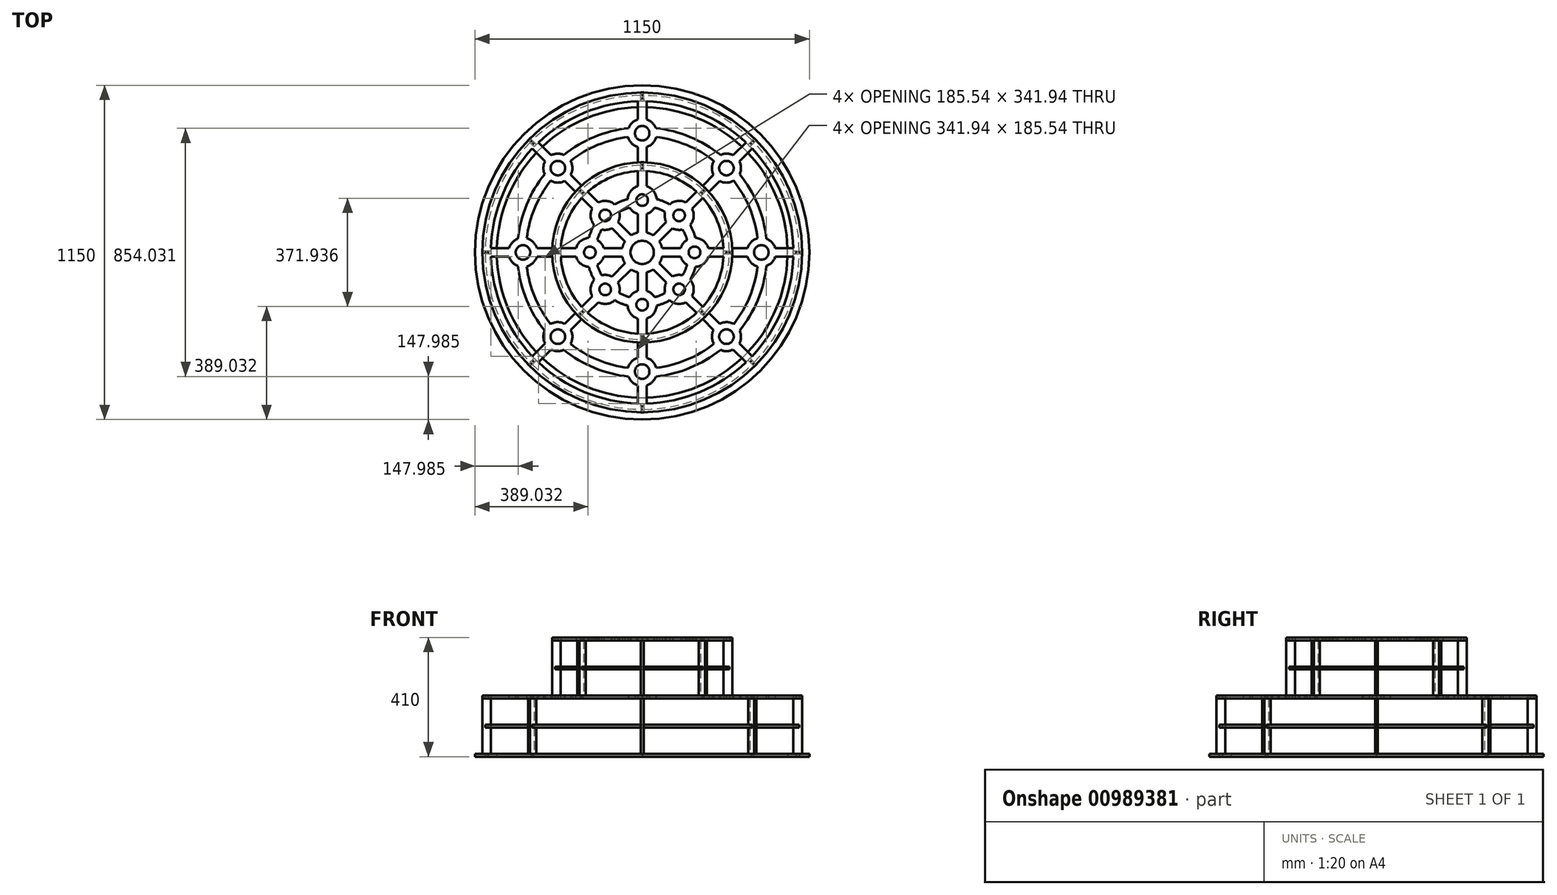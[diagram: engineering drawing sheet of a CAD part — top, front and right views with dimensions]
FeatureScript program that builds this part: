
annotation { "Feature Type Name" : "Feature", "Feature Type Description" : "" }
export const myFeature = defineFeature(function(context is Context, id is Id, definition is map)
    precondition{}
    {
        {
            var Q0;
            Q0=qCreatedBy(makeId("Top.planeOp"),FACE);
            cPlane(context, id + "F0", {"entities" : qUnion([Q0]), "cplaneType" : CPlaneType.OFFSET, "offset" : 200 * mm, "width" : 150 * mm, "height" : 150 * mm});
        }
        {
            var Q0;
            Q0=qCreatedBy(makeId("Top.planeOp"),FACE);
            cPlane(context, id + "F1", {"entities" : qUnion([Q0]), "cplaneType" : CPlaneType.OFFSET, "offset" : 200 * mm, "oppositeDirection" : true, "width" : 150 * mm, "height" : 150 * mm});
        }
        {
            var Q0;
            Q0=qCreatedBy(makeId("Top.planeOp"),FACE);
            cPlane(context, id + "F2", {"entities" : qUnion([Q0]), "cplaneType" : CPlaneType.OFFSET, "offset" : 100 * mm, "oppositeDirection" : true, "width" : 150 * mm, "height" : 150 * mm});
        }
        {
            var Q0;
            Q0=qCreatedBy(makeId("Top.planeOp"),FACE);
            cPlane(context, id + "F3", {"entities" : qUnion([Q0]), "cplaneType" : CPlaneType.OFFSET, "offset" : 100 * mm, "width" : 150 * mm, "height" : 150 * mm});
        }
        {
            var Q0;
            Q0=qCreatedBy(makeId("Top.planeOp"),FACE);
            var sketch = newSketch(context, id + "F4", { "sketchPlane" : qUnion([Q0])});
            skCircle(sketch, "E0", {"center": v(0, 0) * mm, "radius": 550 * mm});
            skArc(sketch, "E1", {"start": v(15, -519.78) * mm, "mid": v(199, -480.42) * mm, "end": v(356.94, -378.15) * mm});
            skArc(sketch, "E2", {"start": v(46.86, -427.44) * mm, "mid": v(164.55, -397.27) * mm, "end": v(269.1, -335.38) * mm});
            skArc(sketch, "E3", {"start": v(48.3, -397.07) * mm, "mid": v(153.07, -369.55) * mm, "end": v(246.62, -314.93) * mm});
            skArc(sketch, "E4", {"start": v(15, -309.64) * mm, "mid": v(118.63, -286.4) * mm, "end": v(208.34, -229.55) * mm});
            skCircle(sketch, "E5", {"center": v(0, 0) * mm, "radius": 280 * mm});
            skCircle(sketch, "E6", {"center": v(0, 0) * mm, "radius": 190 * mm, "construction": true});
            skCircle(sketch, "E7", {"center": v(0, 0) * mm, "radius": 160 * mm, "construction": true});
            skCircle(sketch, "E8", {"center": v(0, 0) * mm, "radius": 40 * mm, "construction": true});
            skCircle(sketch, "E9", {"center": v(0, 0) * mm, "radius": 70 * mm, "construction": true});
            skLineSegment(sketch, "E10", {"start": v(0, 725.48) * mm, "end": v(0, -722.46) * mm, "construction": true});
            skLineSegment(sketch, "E11", {"start": v(-695.44, 0) * mm, "end": v(901.66, 0) * mm, "construction": true});
            skArc(sketch, "E12", {"start": v(-15, -362.3) * mm, "mid": v(-36.11, -375.42) * mm, "end": v(-48.3, -397.07) * mm});
            skCircle(sketch, "E13", {"center": v(0, -410) * mm, "radius": 25 * mm});
            skLineSegment(sketch, "E14", {"start": v(15, -519.78) * mm, "end": v(15, -457.7) * mm});
            skLineSegment(sketch, "E15", {"start": v(-15, -457.7) * mm, "end": v(-15, -519.78) * mm});
            skLineSegment(sketch, "E16", {"start": v(-15, -362.3) * mm, "end": v(-15, -309.64) * mm});
            skLineSegment(sketch, "E17", {"start": v(15, -362.3) * mm, "end": v(15, -309.64) * mm});
            skArc(sketch, "E18.trimOffspring", {"start": v(-46.86, -427.44) * mm, "mid": v(-34.43, -446.26) * mm, "end": v(-15, -457.7) * mm});
            skArc(sketch, "E19.trimOffspring", {"start": v(48.3, -397.07) * mm, "mid": v(36.11, -375.42) * mm, "end": v(15, -362.3) * mm});
            skArc(sketch, "E20.trimOffspring", {"start": v(15, -457.7) * mm, "mid": v(34.43, -446.26) * mm, "end": v(46.86, -427.44) * mm});
            skArc(sketch, "E21.1.0", {"start": v(334.25, -313.03) * mm, "mid": v(339.9, -291.2) * mm, "end": v(335.38, -269.1) * mm});
            skCircle(sketch, "E21.1.1", {"center": v(289.91, -289.91) * mm, "radius": 25 * mm});
            skLineSegment(sketch, "E21.1.2", {"start": v(266.8, -245.58) * mm, "end": v(229.55, -208.34) * mm});
            skLineSegment(sketch, "E21.1.3", {"start": v(245.58, -266.8) * mm, "end": v(208.34, -229.55) * mm});
            skArc(sketch, "E21.1.4", {"start": v(245.58, -266.8) * mm, "mid": v(239.93, -291) * mm, "end": v(246.62, -314.93) * mm});
            skArc(sketch, "E21.1.5", {"start": v(269.1, -335.38) * mm, "mid": v(291.2, -339.9) * mm, "end": v(313.03, -334.25) * mm});
            skArc(sketch, "E21.1.6", {"start": v(314.93, -246.62) * mm, "mid": v(291, -239.93) * mm, "end": v(266.8, -245.58) * mm});
            skLineSegment(sketch, "E21.1.7", {"start": v(378.15, -356.94) * mm, "end": v(334.25, -313.03) * mm});
            skLineSegment(sketch, "E21.1.8", {"start": v(313.03, -334.25) * mm, "end": v(356.94, -378.15) * mm});
            skArc(sketch, "E21.2.0", {"start": v(457.7, 15) * mm, "mid": v(446.26, 34.43) * mm, "end": v(427.44, 46.86) * mm});
            skCircle(sketch, "E21.2.1", {"center": v(410, 0) * mm, "radius": 25 * mm});
            skLineSegment(sketch, "E21.2.2", {"start": v(362.3, 15) * mm, "end": v(309.64, 15) * mm});
            skLineSegment(sketch, "E21.2.3", {"start": v(362.3, -15) * mm, "end": v(309.64, -15) * mm});
            skArc(sketch, "E21.2.4", {"start": v(362.3, -15) * mm, "mid": v(375.42, -36.11) * mm, "end": v(397.07, -48.3) * mm});
            skArc(sketch, "E21.2.5", {"start": v(427.44, -46.86) * mm, "mid": v(446.26, -34.43) * mm, "end": v(457.7, -15) * mm});
            skArc(sketch, "E21.2.6", {"start": v(397.07, 48.3) * mm, "mid": v(375.42, 36.11) * mm, "end": v(362.3, 15) * mm});
            skLineSegment(sketch, "E21.2.7", {"start": v(519.78, 15) * mm, "end": v(457.7, 15) * mm});
            skLineSegment(sketch, "E21.2.8", {"start": v(457.7, -15) * mm, "end": v(519.78, -15) * mm});
            skArc(sketch, "E21.3.0", {"start": v(313.03, 334.25) * mm, "mid": v(291.2, 339.9) * mm, "end": v(269.1, 335.38) * mm});
            skCircle(sketch, "E21.3.1", {"center": v(289.91, 289.91) * mm, "radius": 25 * mm});
            skLineSegment(sketch, "E21.3.2", {"start": v(245.58, 266.8) * mm, "end": v(208.34, 229.55) * mm});
            skLineSegment(sketch, "E21.3.3", {"start": v(266.8, 245.58) * mm, "end": v(229.55, 208.34) * mm});
            skArc(sketch, "E21.3.4", {"start": v(266.8, 245.58) * mm, "mid": v(291, 239.93) * mm, "end": v(314.93, 246.62) * mm});
            skArc(sketch, "E21.3.5", {"start": v(335.38, 269.1) * mm, "mid": v(339.9, 291.2) * mm, "end": v(334.25, 313.03) * mm});
            skArc(sketch, "E21.3.6", {"start": v(246.62, 314.93) * mm, "mid": v(239.93, 291) * mm, "end": v(245.58, 266.8) * mm});
            skLineSegment(sketch, "E21.3.7", {"start": v(356.94, 378.15) * mm, "end": v(313.03, 334.25) * mm});
            skLineSegment(sketch, "E21.3.8", {"start": v(334.25, 313.03) * mm, "end": v(378.15, 356.94) * mm});
            skArc(sketch, "E21.4.0", {"start": v(-15, 457.7) * mm, "mid": v(-34.43, 446.26) * mm, "end": v(-46.86, 427.44) * mm});
            skCircle(sketch, "E21.4.1", {"center": v(0, 410) * mm, "radius": 25 * mm});
            skLineSegment(sketch, "E21.4.2", {"start": v(-15, 362.3) * mm, "end": v(-15, 309.64) * mm});
            skLineSegment(sketch, "E21.4.3", {"start": v(15, 362.3) * mm, "end": v(15, 309.64) * mm});
            skArc(sketch, "E21.4.4", {"start": v(15, 362.3) * mm, "mid": v(36.11, 375.42) * mm, "end": v(48.3, 397.07) * mm});
            skArc(sketch, "E21.4.5", {"start": v(46.86, 427.44) * mm, "mid": v(34.43, 446.26) * mm, "end": v(15, 457.7) * mm});
            skArc(sketch, "E21.4.6", {"start": v(-48.3, 397.07) * mm, "mid": v(-36.11, 375.42) * mm, "end": v(-15, 362.3) * mm});
            skLineSegment(sketch, "E21.4.7", {"start": v(-15, 519.78) * mm, "end": v(-15, 457.7) * mm});
            skLineSegment(sketch, "E21.4.8", {"start": v(15, 457.7) * mm, "end": v(15, 519.78) * mm});
            skArc(sketch, "E21.5.0", {"start": v(-334.25, 313.03) * mm, "mid": v(-339.9, 291.2) * mm, "end": v(-335.38, 269.1) * mm});
            skCircle(sketch, "E21.5.1", {"center": v(-289.91, 289.91) * mm, "radius": 25 * mm});
            skLineSegment(sketch, "E21.5.2", {"start": v(-266.8, 245.58) * mm, "end": v(-229.55, 208.34) * mm});
            skLineSegment(sketch, "E21.5.3", {"start": v(-245.58, 266.8) * mm, "end": v(-208.34, 229.55) * mm});
            skArc(sketch, "E21.5.4", {"start": v(-245.58, 266.8) * mm, "mid": v(-239.93, 291) * mm, "end": v(-246.62, 314.93) * mm});
            skArc(sketch, "E21.5.5", {"start": v(-269.1, 335.38) * mm, "mid": v(-291.2, 339.9) * mm, "end": v(-313.03, 334.25) * mm});
            skArc(sketch, "E21.5.6", {"start": v(-314.93, 246.62) * mm, "mid": v(-291, 239.93) * mm, "end": v(-266.8, 245.58) * mm});
            skLineSegment(sketch, "E21.5.7", {"start": v(-378.15, 356.94) * mm, "end": v(-334.25, 313.03) * mm});
            skLineSegment(sketch, "E21.5.8", {"start": v(-313.03, 334.25) * mm, "end": v(-356.94, 378.15) * mm});
            skArc(sketch, "E21.6.0", {"start": v(-457.7, -15) * mm, "mid": v(-446.26, -34.43) * mm, "end": v(-427.44, -46.86) * mm});
            skCircle(sketch, "E21.6.1", {"center": v(-410, 0) * mm, "radius": 25 * mm});
            skLineSegment(sketch, "E21.6.2", {"start": v(-362.3, -15) * mm, "end": v(-309.64, -15) * mm});
            skLineSegment(sketch, "E21.6.3", {"start": v(-362.3, 15) * mm, "end": v(-309.64, 15) * mm});
            skArc(sketch, "E21.6.4", {"start": v(-362.3, 15) * mm, "mid": v(-375.42, 36.11) * mm, "end": v(-397.07, 48.3) * mm});
            skArc(sketch, "E21.6.5", {"start": v(-427.44, 46.86) * mm, "mid": v(-446.26, 34.43) * mm, "end": v(-457.7, 15) * mm});
            skArc(sketch, "E21.6.6", {"start": v(-397.07, -48.3) * mm, "mid": v(-375.42, -36.11) * mm, "end": v(-362.3, -15) * mm});
            skLineSegment(sketch, "E21.6.7", {"start": v(-519.78, -15) * mm, "end": v(-457.7, -15) * mm});
            skLineSegment(sketch, "E21.6.8", {"start": v(-457.7, 15) * mm, "end": v(-519.78, 15) * mm});
            skArc(sketch, "E21.7.0", {"start": v(-313.03, -334.25) * mm, "mid": v(-291.2, -339.9) * mm, "end": v(-269.1, -335.38) * mm});
            skCircle(sketch, "E21.7.1", {"center": v(-289.91, -289.91) * mm, "radius": 25 * mm});
            skLineSegment(sketch, "E21.7.2", {"start": v(-245.58, -266.8) * mm, "end": v(-208.34, -229.55) * mm});
            skLineSegment(sketch, "E21.7.3", {"start": v(-266.8, -245.58) * mm, "end": v(-229.55, -208.34) * mm});
            skArc(sketch, "E21.7.4", {"start": v(-266.8, -245.58) * mm, "mid": v(-291, -239.93) * mm, "end": v(-314.93, -246.62) * mm});
            skArc(sketch, "E21.7.5", {"start": v(-335.38, -269.1) * mm, "mid": v(-339.9, -291.2) * mm, "end": v(-334.25, -313.03) * mm});
            skArc(sketch, "E21.7.6", {"start": v(-246.62, -314.93) * mm, "mid": v(-239.93, -291) * mm, "end": v(-245.58, -266.8) * mm});
            skLineSegment(sketch, "E21.7.7", {"start": v(-356.94, -378.15) * mm, "end": v(-313.03, -334.25) * mm});
            skLineSegment(sketch, "E21.7.8", {"start": v(-334.25, -313.03) * mm, "end": v(-378.15, -356.94) * mm});
            skArc(sketch, "E22.trimOffspring", {"start": v(-246.62, -314.93) * mm, "mid": v(-153.07, -369.55) * mm, "end": v(-48.3, -397.07) * mm});
            skArc(sketch, "E23.trimOffspring", {"start": v(-269.1, -335.38) * mm, "mid": v(-164.55, -397.27) * mm, "end": v(-46.86, -427.44) * mm});
            skArc(sketch, "E24.trimOffspring", {"start": v(-356.94, -378.15) * mm, "mid": v(-199, -480.42) * mm, "end": v(-15, -519.78) * mm});
            skArc(sketch, "E25.trimOffspring", {"start": v(-208.34, -229.55) * mm, "mid": v(-118.63, -286.4) * mm, "end": v(-15, -309.64) * mm});
            skArc(sketch, "E26.trimOffspring", {"start": v(-397.07, -48.3) * mm, "mid": v(-369.55, -153.07) * mm, "end": v(-314.93, -246.62) * mm});
            skArc(sketch, "E27.trimOffspring", {"start": v(-427.44, -46.86) * mm, "mid": v(-397.27, -164.55) * mm, "end": v(-335.38, -269.1) * mm});
            skArc(sketch, "E28.trimOffspring", {"start": v(-309.64, -15) * mm, "mid": v(-286.4, -118.63) * mm, "end": v(-229.55, -208.34) * mm});
            skArc(sketch, "E29.trimOffspring", {"start": v(-519.78, -15) * mm, "mid": v(-480.42, -199) * mm, "end": v(-378.15, -356.94) * mm});
            skArc(sketch, "E30.trimOffspring", {"start": v(-314.93, 246.62) * mm, "mid": v(-369.55, 153.07) * mm, "end": v(-397.07, 48.3) * mm});
            skArc(sketch, "E31.trimOffspring", {"start": v(-335.38, 269.1) * mm, "mid": v(-397.27, 164.55) * mm, "end": v(-427.44, 46.86) * mm});
            skArc(sketch, "E32.trimOffspring", {"start": v(-378.15, 356.94) * mm, "mid": v(-480.42, 199) * mm, "end": v(-519.78, 15) * mm});
            skArc(sketch, "E33.trimOffspring", {"start": v(-229.55, 208.34) * mm, "mid": v(-286.4, 118.63) * mm, "end": v(-309.64, 15) * mm});
            skArc(sketch, "E34.trimOffspring", {"start": v(-15, 309.64) * mm, "mid": v(-118.63, 286.4) * mm, "end": v(-208.34, 229.55) * mm});
            skArc(sketch, "E35.trimOffspring", {"start": v(-48.3, 397.07) * mm, "mid": v(-153.07, 369.55) * mm, "end": v(-246.62, 314.93) * mm});
            skArc(sketch, "E36.trimOffspring", {"start": v(-46.86, 427.44) * mm, "mid": v(-164.55, 397.27) * mm, "end": v(-269.1, 335.38) * mm});
            skArc(sketch, "E37.trimOffspring", {"start": v(-15, 519.78) * mm, "mid": v(-199, 480.42) * mm, "end": v(-356.94, 378.15) * mm});
            skArc(sketch, "E38.trimOffspring", {"start": v(269.1, 335.38) * mm, "mid": v(164.55, 397.27) * mm, "end": v(46.86, 427.44) * mm});
            skArc(sketch, "E39.trimOffspring", {"start": v(246.62, 314.93) * mm, "mid": v(153.07, 369.55) * mm, "end": v(48.3, 397.07) * mm});
            skArc(sketch, "E40.trimOffspring", {"start": v(208.34, 229.55) * mm, "mid": v(118.63, 286.4) * mm, "end": v(15, 309.64) * mm});
            skArc(sketch, "E41.trimOffspring", {"start": v(356.94, 378.15) * mm, "mid": v(199, 480.42) * mm, "end": v(15, 519.78) * mm});
            skArc(sketch, "E42.trimOffspring", {"start": v(309.64, 15) * mm, "mid": v(286.4, 118.63) * mm, "end": v(229.55, 208.34) * mm});
            skArc(sketch, "E43.trimOffspring", {"start": v(397.07, 48.3) * mm, "mid": v(369.55, 153.07) * mm, "end": v(314.93, 246.62) * mm});
            skArc(sketch, "E44.trimOffspring", {"start": v(427.44, 46.86) * mm, "mid": v(397.27, 164.55) * mm, "end": v(335.38, 269.1) * mm});
            skArc(sketch, "E45.trimOffspring", {"start": v(519.78, 15) * mm, "mid": v(480.42, 199) * mm, "end": v(378.15, 356.94) * mm});
            skArc(sketch, "E46.trimOffspring", {"start": v(335.38, -269.1) * mm, "mid": v(397.27, -164.55) * mm, "end": v(427.44, -46.86) * mm});
            skArc(sketch, "E47.trimOffspring", {"start": v(314.93, -246.62) * mm, "mid": v(369.55, -153.07) * mm, "end": v(397.07, -48.3) * mm});
            skArc(sketch, "E48.trimOffspring", {"start": v(378.15, -356.94) * mm, "mid": v(480.42, -199) * mm, "end": v(519.78, -15) * mm});
            skArc(sketch, "E49.trimOffspring", {"start": v(229.55, -208.34) * mm, "mid": v(286.4, -118.63) * mm, "end": v(309.64, -15) * mm});
            skLineSegment(sketch, "E50.bottom", {"start": v(4.9, 530) * mm, "end": v(1, 530) * mm});
            skLineSegment(sketch, "E50.top", {"start": v(4.9, 540) * mm, "end": v(1, 540) * mm});
            skLineSegment(sketch, "E50.left", {"start": v(4.9, 530) * mm, "end": v(4.9, 540) * mm});
            skLineSegment(sketch, "E50.right", {"start": v(-4.9, 530) * mm, "end": v(-4.9, 540) * mm});
            skPoint(sketch, "E50.middle", {"position": v(0, 535) * mm});
            skLineSegment(sketch, "E51", {"start": v(0, 541) * mm, "end": v(-1, 540) * mm});
            skLineSegment(sketch, "E52", {"start": v(0, 541) * mm, "end": v(1, 540) * mm});
            skLineSegment(sketch, "E53.trimOffspring", {"start": v(-1, 540) * mm, "end": v(-4.9, 540) * mm});
            skLineSegment(sketch, "E54", {"start": v(0, 529) * mm, "end": v(-1, 530) * mm});
            skLineSegment(sketch, "E55", {"start": v(0, 529) * mm, "end": v(1, 530) * mm});
            skLineSegment(sketch, "E56.trimOffspring", {"start": v(-1, 530) * mm, "end": v(-4.9, 530) * mm});
            skPoint(sketch, "E57.1.0", {"position": v(-378.3, 378.3) * mm});
            skLineSegment(sketch, "E57.1.1", {"start": v(-378.23, 371.3) * mm, "end": v(-385.3, 378.37) * mm});
            skLineSegment(sketch, "E57.1.2", {"start": v(-371.3, 378.23) * mm, "end": v(-378.37, 385.3) * mm});
            skLineSegment(sketch, "E57.1.3", {"start": v(-371.3, 378.23) * mm, "end": v(-374.06, 375.47) * mm});
            skLineSegment(sketch, "E57.1.4", {"start": v(-374.06, 374.06) * mm, "end": v(-374.06, 375.47) * mm});
            skLineSegment(sketch, "E57.1.5", {"start": v(-374.06, 374.06) * mm, "end": v(-375.47, 374.06) * mm});
            skLineSegment(sketch, "E57.1.6", {"start": v(-375.47, 374.06) * mm, "end": v(-378.23, 371.3) * mm});
            skLineSegment(sketch, "E57.1.7", {"start": v(-378.37, 385.3) * mm, "end": v(-381.13, 382.54) * mm});
            skLineSegment(sketch, "E57.1.8", {"start": v(-382.54, 381.13) * mm, "end": v(-385.3, 378.37) * mm});
            skLineSegment(sketch, "E57.1.9", {"start": v(-382.54, 382.54) * mm, "end": v(-381.13, 382.54) * mm});
            skLineSegment(sketch, "E57.1.10", {"start": v(-382.54, 382.54) * mm, "end": v(-382.54, 381.13) * mm});
            skPoint(sketch, "E57.2.0", {"position": v(-535, 0) * mm});
            skLineSegment(sketch, "E57.2.1", {"start": v(-530, -4.9) * mm, "end": v(-540, -4.9) * mm});
            skLineSegment(sketch, "E57.2.2", {"start": v(-530, 4.9) * mm, "end": v(-540, 4.9) * mm});
            skLineSegment(sketch, "E57.2.3", {"start": v(-530, 4.9) * mm, "end": v(-530, 1) * mm});
            skLineSegment(sketch, "E57.2.4", {"start": v(-529, 0) * mm, "end": v(-530, 1) * mm});
            skLineSegment(sketch, "E57.2.5", {"start": v(-529, 0) * mm, "end": v(-530, -1) * mm});
            skLineSegment(sketch, "E57.2.6", {"start": v(-530, -1) * mm, "end": v(-530, -4.9) * mm});
            skLineSegment(sketch, "E57.2.7", {"start": v(-540, 4.9) * mm, "end": v(-540, 1) * mm});
            skLineSegment(sketch, "E57.2.8", {"start": v(-540, -1) * mm, "end": v(-540, -4.9) * mm});
            skLineSegment(sketch, "E57.2.9", {"start": v(-541, 0) * mm, "end": v(-540, 1) * mm});
            skLineSegment(sketch, "E57.2.10", {"start": v(-541, 0) * mm, "end": v(-540, -1) * mm});
            skPoint(sketch, "E57.3.0", {"position": v(-378.3, -378.3) * mm});
            skLineSegment(sketch, "E57.3.1", {"start": v(-371.3, -378.23) * mm, "end": v(-378.37, -385.3) * mm});
            skLineSegment(sketch, "E57.3.2", {"start": v(-378.23, -371.3) * mm, "end": v(-385.3, -378.37) * mm});
            skLineSegment(sketch, "E57.3.3", {"start": v(-378.23, -371.3) * mm, "end": v(-375.47, -374.06) * mm});
            skLineSegment(sketch, "E57.3.4", {"start": v(-374.06, -374.06) * mm, "end": v(-375.47, -374.06) * mm});
            skLineSegment(sketch, "E57.3.5", {"start": v(-374.06, -374.06) * mm, "end": v(-374.06, -375.47) * mm});
            skLineSegment(sketch, "E57.3.6", {"start": v(-374.06, -375.47) * mm, "end": v(-371.3, -378.23) * mm});
            skLineSegment(sketch, "E57.3.7", {"start": v(-385.3, -378.37) * mm, "end": v(-382.54, -381.13) * mm});
            skLineSegment(sketch, "E57.3.8", {"start": v(-381.13, -382.54) * mm, "end": v(-378.37, -385.3) * mm});
            skLineSegment(sketch, "E57.3.9", {"start": v(-382.54, -382.54) * mm, "end": v(-382.54, -381.13) * mm});
            skLineSegment(sketch, "E57.3.10", {"start": v(-382.54, -382.54) * mm, "end": v(-381.13, -382.54) * mm});
            skPoint(sketch, "E57.4.0", {"position": v(0, -535) * mm});
            skLineSegment(sketch, "E57.4.1", {"start": v(4.9, -530) * mm, "end": v(4.9, -540) * mm});
            skLineSegment(sketch, "E57.4.2", {"start": v(-4.9, -530) * mm, "end": v(-4.9, -540) * mm});
            skLineSegment(sketch, "E57.4.3", {"start": v(-4.9, -530) * mm, "end": v(-1, -530) * mm});
            skLineSegment(sketch, "E57.4.4", {"start": v(0, -529) * mm, "end": v(-1, -530) * mm});
            skLineSegment(sketch, "E57.4.5", {"start": v(0, -529) * mm, "end": v(1, -530) * mm});
            skLineSegment(sketch, "E57.4.6", {"start": v(1, -530) * mm, "end": v(4.9, -530) * mm});
            skLineSegment(sketch, "E57.4.7", {"start": v(-4.9, -540) * mm, "end": v(-1, -540) * mm});
            skLineSegment(sketch, "E57.4.8", {"start": v(1, -540) * mm, "end": v(4.9, -540) * mm});
            skLineSegment(sketch, "E57.4.9", {"start": v(0, -541) * mm, "end": v(-1, -540) * mm});
            skLineSegment(sketch, "E57.4.10", {"start": v(0, -541) * mm, "end": v(1, -540) * mm});
            skPoint(sketch, "E57.5.0", {"position": v(378.3, -378.3) * mm});
            skLineSegment(sketch, "E57.5.1", {"start": v(378.23, -371.3) * mm, "end": v(385.3, -378.37) * mm});
            skLineSegment(sketch, "E57.5.2", {"start": v(371.3, -378.23) * mm, "end": v(378.37, -385.3) * mm});
            skLineSegment(sketch, "E57.5.3", {"start": v(371.3, -378.23) * mm, "end": v(374.06, -375.47) * mm});
            skLineSegment(sketch, "E57.5.4", {"start": v(374.06, -374.06) * mm, "end": v(374.06, -375.47) * mm});
            skLineSegment(sketch, "E57.5.5", {"start": v(374.06, -374.06) * mm, "end": v(375.47, -374.06) * mm});
            skLineSegment(sketch, "E57.5.6", {"start": v(375.47, -374.06) * mm, "end": v(378.23, -371.3) * mm});
            skLineSegment(sketch, "E57.5.7", {"start": v(378.37, -385.3) * mm, "end": v(381.13, -382.54) * mm});
            skLineSegment(sketch, "E57.5.8", {"start": v(382.54, -381.13) * mm, "end": v(385.3, -378.37) * mm});
            skLineSegment(sketch, "E57.5.9", {"start": v(382.54, -382.54) * mm, "end": v(381.13, -382.54) * mm});
            skLineSegment(sketch, "E57.5.10", {"start": v(382.54, -382.54) * mm, "end": v(382.54, -381.13) * mm});
            skPoint(sketch, "E57.6.0", {"position": v(535, 0) * mm});
            skLineSegment(sketch, "E57.6.1", {"start": v(530, 4.9) * mm, "end": v(540, 4.9) * mm});
            skLineSegment(sketch, "E57.6.2", {"start": v(530, -4.9) * mm, "end": v(540, -4.9) * mm});
            skLineSegment(sketch, "E57.6.3", {"start": v(530, -4.9) * mm, "end": v(530, -1) * mm});
            skLineSegment(sketch, "E57.6.4", {"start": v(529, 0) * mm, "end": v(530, -1) * mm});
            skLineSegment(sketch, "E57.6.5", {"start": v(529, 0) * mm, "end": v(530, 1) * mm});
            skLineSegment(sketch, "E57.6.6", {"start": v(530, 1) * mm, "end": v(530, 4.9) * mm});
            skLineSegment(sketch, "E57.6.7", {"start": v(540, -4.9) * mm, "end": v(540, -1) * mm});
            skLineSegment(sketch, "E57.6.8", {"start": v(540, 1) * mm, "end": v(540, 4.9) * mm});
            skLineSegment(sketch, "E57.6.9", {"start": v(541, 0) * mm, "end": v(540, -1) * mm});
            skLineSegment(sketch, "E57.6.10", {"start": v(541, 0) * mm, "end": v(540, 1) * mm});
            skPoint(sketch, "E57.7.0", {"position": v(378.3, 378.3) * mm});
            skLineSegment(sketch, "E57.7.1", {"start": v(371.3, 378.23) * mm, "end": v(378.37, 385.3) * mm});
            skLineSegment(sketch, "E57.7.2", {"start": v(378.23, 371.3) * mm, "end": v(385.3, 378.37) * mm});
            skLineSegment(sketch, "E57.7.3", {"start": v(378.23, 371.3) * mm, "end": v(375.47, 374.06) * mm});
            skLineSegment(sketch, "E57.7.4", {"start": v(374.06, 374.06) * mm, "end": v(375.47, 374.06) * mm});
            skLineSegment(sketch, "E57.7.5", {"start": v(374.06, 374.06) * mm, "end": v(374.06, 375.47) * mm});
            skLineSegment(sketch, "E57.7.6", {"start": v(374.06, 375.47) * mm, "end": v(371.3, 378.23) * mm});
            skLineSegment(sketch, "E57.7.7", {"start": v(385.3, 378.37) * mm, "end": v(382.54, 381.13) * mm});
            skLineSegment(sketch, "E57.7.8", {"start": v(381.13, 382.54) * mm, "end": v(378.37, 385.3) * mm});
            skLineSegment(sketch, "E57.7.9", {"start": v(382.54, 382.54) * mm, "end": v(382.54, 381.13) * mm});
            skLineSegment(sketch, "E57.7.10", {"start": v(382.54, 382.54) * mm, "end": v(381.13, 382.54) * mm});
            skLineSegment(sketch, "E58.bottom", {"start": v(4.9, 290) * mm, "end": v(1, 290) * mm});
            skLineSegment(sketch, "E58.top", {"start": v(4.9, 300) * mm, "end": v(1, 300) * mm});
            skLineSegment(sketch, "E58.left", {"start": v(4.9, 290) * mm, "end": v(4.9, 300) * mm});
            skLineSegment(sketch, "E58.right", {"start": v(-4.9, 290) * mm, "end": v(-4.9, 300) * mm});
            skPoint(sketch, "E58.middle", {"position": v(0, 295) * mm});
            skLineSegment(sketch, "E59", {"start": v(0, 301) * mm, "end": v(-1, 300) * mm});
            skLineSegment(sketch, "E60", {"start": v(0, 301) * mm, "end": v(1, 300) * mm});
            skLineSegment(sketch, "E61.trimOffspring", {"start": v(-1, 300) * mm, "end": v(-4.9, 300) * mm});
            skLineSegment(sketch, "E62", {"start": v(0, 289) * mm, "end": v(-1, 290) * mm});
            skLineSegment(sketch, "E63", {"start": v(0, 289) * mm, "end": v(1, 290) * mm});
            skLineSegment(sketch, "E64.trimOffspring", {"start": v(-1, 290) * mm, "end": v(-4.9, 290) * mm});
            skLineSegment(sketch, "E65.1.0", {"start": v(-201.6, 208.53) * mm, "end": v(-208.67, 215.6) * mm});
            skPoint(sketch, "E65.1.1", {"position": v(-208.6, 208.6) * mm});
            skLineSegment(sketch, "E65.1.2", {"start": v(-208.53, 201.6) * mm, "end": v(-215.6, 208.67) * mm});
            skLineSegment(sketch, "E65.1.3", {"start": v(-205.77, 204.35) * mm, "end": v(-208.53, 201.6) * mm});
            skLineSegment(sketch, "E65.1.4", {"start": v(-208.67, 215.6) * mm, "end": v(-211.42, 212.84) * mm});
            skLineSegment(sketch, "E65.1.5", {"start": v(-201.6, 208.53) * mm, "end": v(-204.35, 205.77) * mm});
            skLineSegment(sketch, "E65.1.6", {"start": v(-212.84, 211.42) * mm, "end": v(-215.6, 208.67) * mm});
            skLineSegment(sketch, "E65.1.7", {"start": v(-204.35, 204.35) * mm, "end": v(-205.77, 204.35) * mm});
            skLineSegment(sketch, "E65.1.8", {"start": v(-212.84, 212.84) * mm, "end": v(-211.42, 212.84) * mm});
            skLineSegment(sketch, "E65.1.9", {"start": v(-212.84, 212.84) * mm, "end": v(-212.84, 211.42) * mm});
            skLineSegment(sketch, "E65.1.10", {"start": v(-204.35, 204.35) * mm, "end": v(-204.35, 205.77) * mm});
            skLineSegment(sketch, "E65.2.0", {"start": v(-290, 4.9) * mm, "end": v(-300, 4.9) * mm});
            skPoint(sketch, "E65.2.1", {"position": v(-295, 0) * mm});
            skLineSegment(sketch, "E65.2.2", {"start": v(-290, -4.9) * mm, "end": v(-300, -4.9) * mm});
            skLineSegment(sketch, "E65.2.3", {"start": v(-290, -1) * mm, "end": v(-290, -4.9) * mm});
            skLineSegment(sketch, "E65.2.4", {"start": v(-300, 4.9) * mm, "end": v(-300, 1) * mm});
            skLineSegment(sketch, "E65.2.5", {"start": v(-290, 4.9) * mm, "end": v(-290, 1) * mm});
            skLineSegment(sketch, "E65.2.6", {"start": v(-300, -1) * mm, "end": v(-300, -4.9) * mm});
            skLineSegment(sketch, "E65.2.7", {"start": v(-289, 0) * mm, "end": v(-290, -1) * mm});
            skLineSegment(sketch, "E65.2.8", {"start": v(-301, 0) * mm, "end": v(-300, 1) * mm});
            skLineSegment(sketch, "E65.2.9", {"start": v(-301, 0) * mm, "end": v(-300, -1) * mm});
            skLineSegment(sketch, "E65.2.10", {"start": v(-289, 0) * mm, "end": v(-290, 1) * mm});
            skLineSegment(sketch, "E65.3.0", {"start": v(-208.53, -201.6) * mm, "end": v(-215.6, -208.67) * mm});
            skPoint(sketch, "E65.3.1", {"position": v(-208.6, -208.6) * mm});
            skLineSegment(sketch, "E65.3.2", {"start": v(-201.6, -208.53) * mm, "end": v(-208.67, -215.6) * mm});
            skLineSegment(sketch, "E65.3.3", {"start": v(-204.35, -205.77) * mm, "end": v(-201.6, -208.53) * mm});
            skLineSegment(sketch, "E65.3.4", {"start": v(-215.6, -208.67) * mm, "end": v(-212.84, -211.42) * mm});
            skLineSegment(sketch, "E65.3.5", {"start": v(-208.53, -201.6) * mm, "end": v(-205.77, -204.35) * mm});
            skLineSegment(sketch, "E65.3.6", {"start": v(-211.42, -212.84) * mm, "end": v(-208.67, -215.6) * mm});
            skLineSegment(sketch, "E65.3.7", {"start": v(-204.35, -204.35) * mm, "end": v(-204.35, -205.77) * mm});
            skLineSegment(sketch, "E65.3.8", {"start": v(-212.84, -212.84) * mm, "end": v(-212.84, -211.42) * mm});
            skLineSegment(sketch, "E65.3.9", {"start": v(-212.84, -212.84) * mm, "end": v(-211.42, -212.84) * mm});
            skLineSegment(sketch, "E65.3.10", {"start": v(-204.35, -204.35) * mm, "end": v(-205.77, -204.35) * mm});
            skLineSegment(sketch, "E65.4.0", {"start": v(-4.9, -290) * mm, "end": v(-4.9, -300) * mm});
            skPoint(sketch, "E65.4.1", {"position": v(0, -295) * mm});
            skLineSegment(sketch, "E65.4.2", {"start": v(4.9, -290) * mm, "end": v(4.9, -300) * mm});
            skLineSegment(sketch, "E65.4.3", {"start": v(1, -290) * mm, "end": v(4.9, -290) * mm});
            skLineSegment(sketch, "E65.4.4", {"start": v(-4.9, -300) * mm, "end": v(-1, -300) * mm});
            skLineSegment(sketch, "E65.4.5", {"start": v(-4.9, -290) * mm, "end": v(-1, -290) * mm});
            skLineSegment(sketch, "E65.4.6", {"start": v(1, -300) * mm, "end": v(4.9, -300) * mm});
            skLineSegment(sketch, "E65.4.7", {"start": v(0, -289) * mm, "end": v(1, -290) * mm});
            skLineSegment(sketch, "E65.4.8", {"start": v(0, -301) * mm, "end": v(-1, -300) * mm});
            skLineSegment(sketch, "E65.4.9", {"start": v(0, -301) * mm, "end": v(1, -300) * mm});
            skLineSegment(sketch, "E65.4.10", {"start": v(0, -289) * mm, "end": v(-1, -290) * mm});
            skLineSegment(sketch, "E65.5.0", {"start": v(201.6, -208.53) * mm, "end": v(208.67, -215.6) * mm});
            skPoint(sketch, "E65.5.1", {"position": v(208.6, -208.6) * mm});
            skLineSegment(sketch, "E65.5.2", {"start": v(208.53, -201.6) * mm, "end": v(215.6, -208.67) * mm});
            skLineSegment(sketch, "E65.5.3", {"start": v(205.77, -204.35) * mm, "end": v(208.53, -201.6) * mm});
            skLineSegment(sketch, "E65.5.4", {"start": v(208.67, -215.6) * mm, "end": v(211.42, -212.84) * mm});
            skLineSegment(sketch, "E65.5.5", {"start": v(201.6, -208.53) * mm, "end": v(204.35, -205.77) * mm});
            skLineSegment(sketch, "E65.5.6", {"start": v(212.84, -211.42) * mm, "end": v(215.6, -208.67) * mm});
            skLineSegment(sketch, "E65.5.7", {"start": v(204.35, -204.35) * mm, "end": v(205.77, -204.35) * mm});
            skLineSegment(sketch, "E65.5.8", {"start": v(212.84, -212.84) * mm, "end": v(211.42, -212.84) * mm});
            skLineSegment(sketch, "E65.5.9", {"start": v(212.84, -212.84) * mm, "end": v(212.84, -211.42) * mm});
            skLineSegment(sketch, "E65.5.10", {"start": v(204.35, -204.35) * mm, "end": v(204.35, -205.77) * mm});
            skLineSegment(sketch, "E65.6.0", {"start": v(290, -4.9) * mm, "end": v(300, -4.9) * mm});
            skPoint(sketch, "E65.6.1", {"position": v(295, 0) * mm});
            skLineSegment(sketch, "E65.6.2", {"start": v(290, 4.9) * mm, "end": v(300, 4.9) * mm});
            skLineSegment(sketch, "E65.6.3", {"start": v(290, 1) * mm, "end": v(290, 4.9) * mm});
            skLineSegment(sketch, "E65.6.4", {"start": v(300, -4.9) * mm, "end": v(300, -1) * mm});
            skLineSegment(sketch, "E65.6.5", {"start": v(290, -4.9) * mm, "end": v(290, -1) * mm});
            skLineSegment(sketch, "E65.6.6", {"start": v(300, 1) * mm, "end": v(300, 4.9) * mm});
            skLineSegment(sketch, "E65.6.7", {"start": v(289, 0) * mm, "end": v(290, 1) * mm});
            skLineSegment(sketch, "E65.6.8", {"start": v(301, 0) * mm, "end": v(300, -1) * mm});
            skLineSegment(sketch, "E65.6.9", {"start": v(301, 0) * mm, "end": v(300, 1) * mm});
            skLineSegment(sketch, "E65.6.10", {"start": v(289, 0) * mm, "end": v(290, -1) * mm});
            skLineSegment(sketch, "E65.7.0", {"start": v(208.53, 201.6) * mm, "end": v(215.6, 208.67) * mm});
            skPoint(sketch, "E65.7.1", {"position": v(208.6, 208.6) * mm});
            skLineSegment(sketch, "E65.7.2", {"start": v(201.6, 208.53) * mm, "end": v(208.67, 215.6) * mm});
            skLineSegment(sketch, "E65.7.3", {"start": v(204.35, 205.77) * mm, "end": v(201.6, 208.53) * mm});
            skLineSegment(sketch, "E65.7.4", {"start": v(215.6, 208.67) * mm, "end": v(212.84, 211.42) * mm});
            skLineSegment(sketch, "E65.7.5", {"start": v(208.53, 201.6) * mm, "end": v(205.77, 204.35) * mm});
            skLineSegment(sketch, "E65.7.6", {"start": v(211.42, 212.84) * mm, "end": v(208.67, 215.6) * mm});
            skLineSegment(sketch, "E65.7.7", {"start": v(204.35, 204.35) * mm, "end": v(204.35, 205.77) * mm});
            skLineSegment(sketch, "E65.7.8", {"start": v(212.84, 212.84) * mm, "end": v(212.84, 211.42) * mm});
            skLineSegment(sketch, "E65.7.9", {"start": v(212.84, 212.84) * mm, "end": v(211.42, 212.84) * mm});
            skLineSegment(sketch, "E65.7.10", {"start": v(204.35, 204.35) * mm, "end": v(205.77, 204.35) * mm});
            skSolve(sketch);
        }
        {
            var Q0;
            Q0=qSketchRegion(id+"F4",true);
            extrude(context, id + "F5", {"entities" : qUnion([Q0]), "depth" : 10 * mm, "offsetDistance" : 25 * mm});
        }
        {
            var Q0;
            Q0=qCreatedBy(id+"F0.planeOp",FACE);
            var sketch = newSketch(context, id + "F6", { "sketchPlane" : qUnion([Q0])});
            skArc(sketch, "E66.0", {"start": v(42.8, -154.17) * mm, "mid": v(61.23, -147.82) * mm, "end": v(78.74, -139.28) * mm});
            skArc(sketch, "E67.0", {"start": v(49.89, -183.33) * mm, "mid": v(72.7, -175.54) * mm, "end": v(94.36, -164.91) * mm});
            skArc(sketch, "E68.0", {"start": v(15, -279.6) * mm, "mid": v(107.15, -258.69) * mm, "end": v(187.1, -208.31) * mm});
            skArc(sketch, "E69.0", {"start": v(15, -68.37) * mm, "mid": v(26.79, -64.67) * mm, "end": v(37.74, -58.95) * mm});
            skCircle(sketch, "E70.0", {"center": v(0, 0) * mm, "radius": 40 * mm});
            skPoint(sketch, "E71.0", {"position": v(15, 309.64) * mm});
            skCircle(sketch, "E72", {"center": v(0, 0) * mm, "radius": 310 * mm});
            skArc(sketch, "E73", {"start": v(-15, -132.3) * mm, "mid": v(-30.9, -140.7) * mm, "end": v(-42.8, -154.17) * mm});
            skCircle(sketch, "E74", {"center": v(0, -180) * mm, "radius": 20 * mm});
            skLineSegment(sketch, "E75", {"start": v(-15, -68.37) * mm, "end": v(-15, -132.3) * mm});
            skLineSegment(sketch, "E76", {"start": v(15, -68.37) * mm, "end": v(15, -132.3) * mm});
            skLineSegment(sketch, "E77", {"start": v(-15, -227.7) * mm, "end": v(-15, -279.6) * mm});
            skLineSegment(sketch, "E78", {"start": v(15, -227.7) * mm, "end": v(15, -279.6) * mm});
            skArc(sketch, "E79.trimOffspring", {"start": v(42.8, -154.17) * mm, "mid": v(30.9, -140.7) * mm, "end": v(15, -132.3) * mm});
            skArc(sketch, "E80.trimOffspring", {"start": v(15, -227.7) * mm, "mid": v(39.3, -210.9) * mm, "end": v(49.89, -183.33) * mm});
            skArc(sketch, "E81.trimOffspring", {"start": v(-49.89, -183.33) * mm, "mid": v(-39.3, -210.9) * mm, "end": v(-15, -227.7) * mm});
            skLineSegment(sketch, "E82.1.0", {"start": v(58.95, -37.74) * mm, "end": v(104.16, -82.95) * mm});
            skLineSegment(sketch, "E82.1.1", {"start": v(37.74, -58.95) * mm, "end": v(82.95, -104.16) * mm});
            skArc(sketch, "E82.1.2", {"start": v(82.95, -104.16) * mm, "mid": v(77.63, -121.34) * mm, "end": v(78.74, -139.28) * mm});
            skCircle(sketch, "E82.1.3", {"center": v(127.28, -127.28) * mm, "radius": 20 * mm});
            skArc(sketch, "E82.1.4", {"start": v(94.36, -164.91) * mm, "mid": v(121.34, -176.93) * mm, "end": v(150.4, -171.61) * mm});
            skArc(sketch, "E82.1.5", {"start": v(171.61, -150.4) * mm, "mid": v(176.93, -121.34) * mm, "end": v(164.91, -94.36) * mm});
            skArc(sketch, "E82.1.6", {"start": v(139.28, -78.74) * mm, "mid": v(121.34, -77.63) * mm, "end": v(104.16, -82.95) * mm});
            skLineSegment(sketch, "E82.1.7", {"start": v(171.61, -150.4) * mm, "end": v(208.31, -187.1) * mm});
            skLineSegment(sketch, "E82.1.8", {"start": v(150.4, -171.61) * mm, "end": v(187.1, -208.31) * mm});
            skLineSegment(sketch, "E82.2.0", {"start": v(68.37, 15) * mm, "end": v(132.3, 15) * mm});
            skLineSegment(sketch, "E82.2.1", {"start": v(68.37, -15) * mm, "end": v(132.3, -15) * mm});
            skArc(sketch, "E82.2.2", {"start": v(132.3, -15) * mm, "mid": v(140.7, -30.9) * mm, "end": v(154.17, -42.8) * mm});
            skCircle(sketch, "E82.2.3", {"center": v(180, 0) * mm, "radius": 20 * mm});
            skArc(sketch, "E82.2.4", {"start": v(183.33, -49.89) * mm, "mid": v(210.9, -39.3) * mm, "end": v(227.7, -15) * mm});
            skArc(sketch, "E82.2.5", {"start": v(227.7, 15) * mm, "mid": v(210.9, 39.3) * mm, "end": v(183.33, 49.89) * mm});
            skArc(sketch, "E82.2.6", {"start": v(154.17, 42.8) * mm, "mid": v(140.7, 30.9) * mm, "end": v(132.3, 15) * mm});
            skLineSegment(sketch, "E82.2.7", {"start": v(227.7, 15) * mm, "end": v(279.6, 15) * mm});
            skLineSegment(sketch, "E82.2.8", {"start": v(227.7, -15) * mm, "end": v(279.6, -15) * mm});
            skLineSegment(sketch, "E82.3.0", {"start": v(37.74, 58.95) * mm, "end": v(82.95, 104.16) * mm});
            skLineSegment(sketch, "E82.3.1", {"start": v(58.95, 37.74) * mm, "end": v(104.16, 82.95) * mm});
            skArc(sketch, "E82.3.2", {"start": v(104.16, 82.95) * mm, "mid": v(121.34, 77.63) * mm, "end": v(139.28, 78.74) * mm});
            skCircle(sketch, "E82.3.3", {"center": v(127.28, 127.28) * mm, "radius": 20 * mm});
            skArc(sketch, "E82.3.4", {"start": v(164.91, 94.36) * mm, "mid": v(176.93, 121.34) * mm, "end": v(171.61, 150.4) * mm});
            skArc(sketch, "E82.3.5", {"start": v(150.4, 171.61) * mm, "mid": v(121.34, 176.93) * mm, "end": v(94.36, 164.91) * mm});
            skArc(sketch, "E82.3.6", {"start": v(78.74, 139.28) * mm, "mid": v(77.63, 121.34) * mm, "end": v(82.95, 104.16) * mm});
            skLineSegment(sketch, "E82.3.7", {"start": v(150.4, 171.61) * mm, "end": v(187.1, 208.31) * mm});
            skLineSegment(sketch, "E82.3.8", {"start": v(171.61, 150.4) * mm, "end": v(208.31, 187.1) * mm});
            skLineSegment(sketch, "E82.4.0", {"start": v(-15, 68.37) * mm, "end": v(-15, 132.3) * mm});
            skLineSegment(sketch, "E82.4.1", {"start": v(15, 68.37) * mm, "end": v(15, 132.3) * mm});
            skArc(sketch, "E82.4.2", {"start": v(15, 132.3) * mm, "mid": v(30.9, 140.7) * mm, "end": v(42.8, 154.17) * mm});
            skCircle(sketch, "E82.4.3", {"center": v(0, 180) * mm, "radius": 20 * mm});
            skArc(sketch, "E82.4.4", {"start": v(49.89, 183.33) * mm, "mid": v(39.3, 210.9) * mm, "end": v(15, 227.7) * mm});
            skArc(sketch, "E82.4.5", {"start": v(-15, 227.7) * mm, "mid": v(-39.3, 210.9) * mm, "end": v(-49.89, 183.33) * mm});
            skArc(sketch, "E82.4.6", {"start": v(-42.8, 154.17) * mm, "mid": v(-30.9, 140.7) * mm, "end": v(-15, 132.3) * mm});
            skLineSegment(sketch, "E82.4.7", {"start": v(-15, 227.7) * mm, "end": v(-15, 279.6) * mm});
            skLineSegment(sketch, "E82.4.8", {"start": v(15, 227.7) * mm, "end": v(15, 279.6) * mm});
            skLineSegment(sketch, "E82.5.0", {"start": v(-58.95, 37.74) * mm, "end": v(-104.16, 82.95) * mm});
            skLineSegment(sketch, "E82.5.1", {"start": v(-37.74, 58.95) * mm, "end": v(-82.95, 104.16) * mm});
            skArc(sketch, "E82.5.2", {"start": v(-82.95, 104.16) * mm, "mid": v(-77.63, 121.34) * mm, "end": v(-78.74, 139.28) * mm});
            skCircle(sketch, "E82.5.3", {"center": v(-127.28, 127.28) * mm, "radius": 20 * mm});
            skArc(sketch, "E82.5.4", {"start": v(-94.36, 164.91) * mm, "mid": v(-121.34, 176.93) * mm, "end": v(-150.4, 171.61) * mm});
            skArc(sketch, "E82.5.5", {"start": v(-171.61, 150.4) * mm, "mid": v(-176.93, 121.34) * mm, "end": v(-164.91, 94.36) * mm});
            skArc(sketch, "E82.5.6", {"start": v(-139.28, 78.74) * mm, "mid": v(-121.34, 77.63) * mm, "end": v(-104.16, 82.95) * mm});
            skLineSegment(sketch, "E82.5.7", {"start": v(-171.61, 150.4) * mm, "end": v(-208.31, 187.1) * mm});
            skLineSegment(sketch, "E82.5.8", {"start": v(-150.4, 171.61) * mm, "end": v(-187.1, 208.31) * mm});
            skLineSegment(sketch, "E82.6.0", {"start": v(-68.37, -15) * mm, "end": v(-132.3, -15) * mm});
            skLineSegment(sketch, "E82.6.1", {"start": v(-68.37, 15) * mm, "end": v(-132.3, 15) * mm});
            skArc(sketch, "E82.6.2", {"start": v(-132.3, 15) * mm, "mid": v(-140.7, 30.9) * mm, "end": v(-154.17, 42.8) * mm});
            skCircle(sketch, "E82.6.3", {"center": v(-180, 0) * mm, "radius": 20 * mm});
            skArc(sketch, "E82.6.4", {"start": v(-183.33, 49.89) * mm, "mid": v(-210.9, 39.3) * mm, "end": v(-227.7, 15) * mm});
            skArc(sketch, "E82.6.5", {"start": v(-227.7, -15) * mm, "mid": v(-210.9, -39.3) * mm, "end": v(-183.33, -49.89) * mm});
            skArc(sketch, "E82.6.6", {"start": v(-154.17, -42.8) * mm, "mid": v(-140.7, -30.9) * mm, "end": v(-132.3, -15) * mm});
            skLineSegment(sketch, "E82.6.7", {"start": v(-227.7, -15) * mm, "end": v(-279.6, -15) * mm});
            skLineSegment(sketch, "E82.6.8", {"start": v(-227.7, 15) * mm, "end": v(-279.6, 15) * mm});
            skLineSegment(sketch, "E82.7.0", {"start": v(-37.74, -58.95) * mm, "end": v(-82.95, -104.16) * mm});
            skLineSegment(sketch, "E82.7.1", {"start": v(-58.95, -37.74) * mm, "end": v(-104.16, -82.95) * mm});
            skArc(sketch, "E82.7.2", {"start": v(-104.16, -82.95) * mm, "mid": v(-121.34, -77.63) * mm, "end": v(-139.28, -78.74) * mm});
            skCircle(sketch, "E82.7.3", {"center": v(-127.28, -127.28) * mm, "radius": 20 * mm});
            skArc(sketch, "E82.7.4", {"start": v(-164.91, -94.36) * mm, "mid": v(-176.93, -121.34) * mm, "end": v(-171.61, -150.4) * mm});
            skArc(sketch, "E82.7.5", {"start": v(-150.4, -171.61) * mm, "mid": v(-121.34, -176.93) * mm, "end": v(-94.36, -164.91) * mm});
            skArc(sketch, "E82.7.6", {"start": v(-78.74, -139.28) * mm, "mid": v(-77.63, -121.34) * mm, "end": v(-82.95, -104.16) * mm});
            skLineSegment(sketch, "E82.7.7", {"start": v(-150.4, -171.61) * mm, "end": v(-187.1, -208.31) * mm});
            skLineSegment(sketch, "E82.7.8", {"start": v(-171.61, -150.4) * mm, "end": v(-208.31, -187.1) * mm});
            skArc(sketch, "E83.trimOffspring", {"start": v(-94.36, -164.91) * mm, "mid": v(-72.7, -175.54) * mm, "end": v(-49.89, -183.33) * mm});
            skArc(sketch, "E84.trimOffspring", {"start": v(-78.74, -139.28) * mm, "mid": v(-61.23, -147.82) * mm, "end": v(-42.8, -154.17) * mm});
            skArc(sketch, "E85.trimOffspring", {"start": v(-187.1, -208.31) * mm, "mid": v(-107.15, -258.69) * mm, "end": v(-15, -279.6) * mm});
            skArc(sketch, "E86.trimOffspring", {"start": v(-37.74, -58.95) * mm, "mid": v(-26.79, -64.67) * mm, "end": v(-15, -68.37) * mm});
            skArc(sketch, "E87.trimOffspring", {"start": v(-68.37, -15) * mm, "mid": v(-64.67, -26.79) * mm, "end": v(-58.95, -37.74) * mm});
            skArc(sketch, "E88.trimOffspring", {"start": v(-154.17, -42.8) * mm, "mid": v(-147.82, -61.23) * mm, "end": v(-139.28, -78.74) * mm});
            skArc(sketch, "E89.trimOffspring", {"start": v(-183.33, -49.89) * mm, "mid": v(-175.54, -72.7) * mm, "end": v(-164.91, -94.36) * mm});
            skArc(sketch, "E90.trimOffspring", {"start": v(-279.6, -15) * mm, "mid": v(-258.69, -107.15) * mm, "end": v(-208.31, -187.1) * mm});
            skArc(sketch, "E91.trimOffspring", {"start": v(-164.91, 94.36) * mm, "mid": v(-175.54, 72.7) * mm, "end": v(-183.33, 49.89) * mm});
            skArc(sketch, "E92.trimOffspring", {"start": v(-139.28, 78.74) * mm, "mid": v(-147.82, 61.23) * mm, "end": v(-154.17, 42.8) * mm});
            skArc(sketch, "E93.trimOffspring", {"start": v(-208.31, 187.1) * mm, "mid": v(-258.69, 107.15) * mm, "end": v(-279.6, 15) * mm});
            skArc(sketch, "E94.trimOffspring", {"start": v(-58.95, 37.74) * mm, "mid": v(-64.67, 26.79) * mm, "end": v(-68.37, 15) * mm});
            skArc(sketch, "E95.trimOffspring", {"start": v(-15, 68.37) * mm, "mid": v(-26.79, 64.67) * mm, "end": v(-37.74, 58.95) * mm});
            skArc(sketch, "E96.trimOffspring", {"start": v(-42.8, 154.17) * mm, "mid": v(-61.23, 147.82) * mm, "end": v(-78.74, 139.28) * mm});
            skArc(sketch, "E97.trimOffspring", {"start": v(-49.89, 183.33) * mm, "mid": v(-72.7, 175.54) * mm, "end": v(-94.36, 164.91) * mm});
            skArc(sketch, "E98.trimOffspring", {"start": v(78.74, 139.28) * mm, "mid": v(61.23, 147.82) * mm, "end": v(42.8, 154.17) * mm});
            skArc(sketch, "E99.trimOffspring", {"start": v(94.36, 164.91) * mm, "mid": v(72.7, 175.54) * mm, "end": v(49.89, 183.33) * mm});
            skArc(sketch, "E100.trimOffspring", {"start": v(183.33, 49.89) * mm, "mid": v(175.54, 72.7) * mm, "end": v(164.91, 94.36) * mm});
            skArc(sketch, "E101.trimOffspring", {"start": v(154.17, 42.8) * mm, "mid": v(147.82, 61.23) * mm, "end": v(139.28, 78.74) * mm});
            skArc(sketch, "E102.trimOffspring", {"start": v(68.37, 15) * mm, "mid": v(64.67, 26.79) * mm, "end": v(58.95, 37.74) * mm});
            skArc(sketch, "E103.trimOffspring", {"start": v(279.6, 15) * mm, "mid": v(258.69, 107.15) * mm, "end": v(208.31, 187.1) * mm});
            skArc(sketch, "E104.trimOffspring", {"start": v(58.95, -37.74) * mm, "mid": v(64.67, -26.79) * mm, "end": v(68.37, -15) * mm});
            skArc(sketch, "E105.trimOffspring", {"start": v(139.28, -78.74) * mm, "mid": v(147.82, -61.23) * mm, "end": v(154.17, -42.8) * mm});
            skArc(sketch, "E106.trimOffspring", {"start": v(164.91, -94.36) * mm, "mid": v(175.54, -72.7) * mm, "end": v(183.33, -49.89) * mm});
            skArc(sketch, "E107.trimOffspring", {"start": v(208.31, -187.1) * mm, "mid": v(258.69, -107.15) * mm, "end": v(279.6, -15) * mm});
            skArc(sketch, "E108.trimOffspring", {"start": v(37.74, 58.95) * mm, "mid": v(26.79, 64.67) * mm, "end": v(15, 68.37) * mm});
            skLineSegment(sketch, "E109.0", {"start": v(-4.9, 290) * mm, "end": v(-4.9, 300) * mm});
            skLineSegment(sketch, "E110.0", {"start": v(-1, 300) * mm, "end": v(-4.9, 300) * mm});
            skLineSegment(sketch, "E111.0", {"start": v(0, 301) * mm, "end": v(-1, 300) * mm});
            skLineSegment(sketch, "E112.0", {"start": v(0, 301) * mm, "end": v(1, 300) * mm});
            skLineSegment(sketch, "E113.0", {"start": v(4.9, 300) * mm, "end": v(1, 300) * mm});
            skLineSegment(sketch, "E114.0", {"start": v(4.9, 290) * mm, "end": v(4.9, 300) * mm});
            skLineSegment(sketch, "E115.0", {"start": v(-1, 290) * mm, "end": v(-4.9, 290) * mm});
            skLineSegment(sketch, "E116.0", {"start": v(0, 289) * mm, "end": v(-1, 290) * mm});
            skLineSegment(sketch, "E117.0", {"start": v(0, 289) * mm, "end": v(1, 290) * mm});
            skLineSegment(sketch, "E118.0", {"start": v(4.9, 290) * mm, "end": v(1, 290) * mm});
            skArc(sketch, "E119.trimOffspring", {"start": v(-15, 279.6) * mm, "mid": v(-107.15, 258.69) * mm, "end": v(-187.1, 208.31) * mm});
            skArc(sketch, "E120.trimOffspring", {"start": v(187.1, 208.31) * mm, "mid": v(107.15, 258.69) * mm, "end": v(15, 279.6) * mm});
            skLineSegment(sketch, "E121.1.0", {"start": v(-205.77, 204.35) * mm, "end": v(-208.53, 201.6) * mm});
            skLineSegment(sketch, "E121.1.1", {"start": v(-208.67, 215.6) * mm, "end": v(-211.42, 212.84) * mm});
            skLineSegment(sketch, "E121.1.2", {"start": v(-201.6, 208.53) * mm, "end": v(-204.35, 205.77) * mm});
            skLineSegment(sketch, "E121.1.3", {"start": v(-212.84, 211.42) * mm, "end": v(-215.6, 208.67) * mm});
            skLineSegment(sketch, "E121.1.4", {"start": v(-208.53, 201.6) * mm, "end": v(-215.6, 208.67) * mm});
            skLineSegment(sketch, "E121.1.5", {"start": v(-201.6, 208.53) * mm, "end": v(-208.67, 215.6) * mm});
            skLineSegment(sketch, "E121.1.6", {"start": v(-212.84, 212.84) * mm, "end": v(-211.42, 212.84) * mm});
            skLineSegment(sketch, "E121.1.7", {"start": v(-204.35, 204.35) * mm, "end": v(-204.35, 205.77) * mm});
            skLineSegment(sketch, "E121.1.8", {"start": v(-204.35, 204.35) * mm, "end": v(-205.77, 204.35) * mm});
            skLineSegment(sketch, "E121.1.9", {"start": v(-212.84, 212.84) * mm, "end": v(-212.84, 211.42) * mm});
            skLineSegment(sketch, "E121.2.0", {"start": v(-290, -1) * mm, "end": v(-290, -4.9) * mm});
            skLineSegment(sketch, "E121.2.1", {"start": v(-300, 4.9) * mm, "end": v(-300, 1) * mm});
            skLineSegment(sketch, "E121.2.2", {"start": v(-290, 4.9) * mm, "end": v(-290, 1) * mm});
            skLineSegment(sketch, "E121.2.3", {"start": v(-300, -1) * mm, "end": v(-300, -4.9) * mm});
            skLineSegment(sketch, "E121.2.4", {"start": v(-290, -4.9) * mm, "end": v(-300, -4.9) * mm});
            skLineSegment(sketch, "E121.2.5", {"start": v(-290, 4.9) * mm, "end": v(-300, 4.9) * mm});
            skLineSegment(sketch, "E121.2.6", {"start": v(-301, 0) * mm, "end": v(-300, 1) * mm});
            skLineSegment(sketch, "E121.2.7", {"start": v(-289, 0) * mm, "end": v(-290, 1) * mm});
            skLineSegment(sketch, "E121.2.8", {"start": v(-289, 0) * mm, "end": v(-290, -1) * mm});
            skLineSegment(sketch, "E121.2.9", {"start": v(-301, 0) * mm, "end": v(-300, -1) * mm});
            skLineSegment(sketch, "E121.3.0", {"start": v(-204.35, -205.77) * mm, "end": v(-201.6, -208.53) * mm});
            skLineSegment(sketch, "E121.3.1", {"start": v(-215.6, -208.67) * mm, "end": v(-212.84, -211.42) * mm});
            skLineSegment(sketch, "E121.3.2", {"start": v(-208.53, -201.6) * mm, "end": v(-205.77, -204.35) * mm});
            skLineSegment(sketch, "E121.3.3", {"start": v(-211.42, -212.84) * mm, "end": v(-208.67, -215.6) * mm});
            skLineSegment(sketch, "E121.3.4", {"start": v(-201.6, -208.53) * mm, "end": v(-208.67, -215.6) * mm});
            skLineSegment(sketch, "E121.3.5", {"start": v(-208.53, -201.6) * mm, "end": v(-215.6, -208.67) * mm});
            skLineSegment(sketch, "E121.3.6", {"start": v(-212.84, -212.84) * mm, "end": v(-212.84, -211.42) * mm});
            skLineSegment(sketch, "E121.3.7", {"start": v(-204.35, -204.35) * mm, "end": v(-205.77, -204.35) * mm});
            skLineSegment(sketch, "E121.3.8", {"start": v(-204.35, -204.35) * mm, "end": v(-204.35, -205.77) * mm});
            skLineSegment(sketch, "E121.3.9", {"start": v(-212.84, -212.84) * mm, "end": v(-211.42, -212.84) * mm});
            skLineSegment(sketch, "E121.4.0", {"start": v(1, -290) * mm, "end": v(4.9, -290) * mm});
            skLineSegment(sketch, "E121.4.1", {"start": v(-4.9, -300) * mm, "end": v(-1, -300) * mm});
            skLineSegment(sketch, "E121.4.2", {"start": v(-4.9, -290) * mm, "end": v(-1, -290) * mm});
            skLineSegment(sketch, "E121.4.3", {"start": v(1, -300) * mm, "end": v(4.9, -300) * mm});
            skLineSegment(sketch, "E121.4.4", {"start": v(4.9, -290) * mm, "end": v(4.9, -300) * mm});
            skLineSegment(sketch, "E121.4.5", {"start": v(-4.9, -290) * mm, "end": v(-4.9, -300) * mm});
            skLineSegment(sketch, "E121.4.6", {"start": v(0, -301) * mm, "end": v(-1, -300) * mm});
            skLineSegment(sketch, "E121.4.7", {"start": v(0, -289) * mm, "end": v(-1, -290) * mm});
            skLineSegment(sketch, "E121.4.8", {"start": v(0, -289) * mm, "end": v(1, -290) * mm});
            skLineSegment(sketch, "E121.4.9", {"start": v(0, -301) * mm, "end": v(1, -300) * mm});
            skLineSegment(sketch, "E121.5.0", {"start": v(205.77, -204.35) * mm, "end": v(208.53, -201.6) * mm});
            skLineSegment(sketch, "E121.5.1", {"start": v(208.67, -215.6) * mm, "end": v(211.42, -212.84) * mm});
            skLineSegment(sketch, "E121.5.2", {"start": v(201.6, -208.53) * mm, "end": v(204.35, -205.77) * mm});
            skLineSegment(sketch, "E121.5.3", {"start": v(212.84, -211.42) * mm, "end": v(215.6, -208.67) * mm});
            skLineSegment(sketch, "E121.5.4", {"start": v(208.53, -201.6) * mm, "end": v(215.6, -208.67) * mm});
            skLineSegment(sketch, "E121.5.5", {"start": v(201.6, -208.53) * mm, "end": v(208.67, -215.6) * mm});
            skLineSegment(sketch, "E121.5.6", {"start": v(212.84, -212.84) * mm, "end": v(211.42, -212.84) * mm});
            skLineSegment(sketch, "E121.5.7", {"start": v(204.35, -204.35) * mm, "end": v(204.35, -205.77) * mm});
            skLineSegment(sketch, "E121.5.8", {"start": v(204.35, -204.35) * mm, "end": v(205.77, -204.35) * mm});
            skLineSegment(sketch, "E121.5.9", {"start": v(212.84, -212.84) * mm, "end": v(212.84, -211.42) * mm});
            skLineSegment(sketch, "E121.6.0", {"start": v(290, 1) * mm, "end": v(290, 4.9) * mm});
            skLineSegment(sketch, "E121.6.1", {"start": v(300, -4.9) * mm, "end": v(300, -1) * mm});
            skLineSegment(sketch, "E121.6.2", {"start": v(290, -4.9) * mm, "end": v(290, -1) * mm});
            skLineSegment(sketch, "E121.6.3", {"start": v(300, 1) * mm, "end": v(300, 4.9) * mm});
            skLineSegment(sketch, "E121.6.4", {"start": v(290, 4.9) * mm, "end": v(300, 4.9) * mm});
            skLineSegment(sketch, "E121.6.5", {"start": v(290, -4.9) * mm, "end": v(300, -4.9) * mm});
            skLineSegment(sketch, "E121.6.6", {"start": v(301, 0) * mm, "end": v(300, -1) * mm});
            skLineSegment(sketch, "E121.6.7", {"start": v(289, 0) * mm, "end": v(290, -1) * mm});
            skLineSegment(sketch, "E121.6.8", {"start": v(289, 0) * mm, "end": v(290, 1) * mm});
            skLineSegment(sketch, "E121.6.9", {"start": v(301, 0) * mm, "end": v(300, 1) * mm});
            skLineSegment(sketch, "E121.7.0", {"start": v(204.35, 205.77) * mm, "end": v(201.6, 208.53) * mm});
            skLineSegment(sketch, "E121.7.1", {"start": v(215.6, 208.67) * mm, "end": v(212.84, 211.42) * mm});
            skLineSegment(sketch, "E121.7.2", {"start": v(208.53, 201.6) * mm, "end": v(205.77, 204.35) * mm});
            skLineSegment(sketch, "E121.7.3", {"start": v(211.42, 212.84) * mm, "end": v(208.67, 215.6) * mm});
            skLineSegment(sketch, "E121.7.4", {"start": v(201.6, 208.53) * mm, "end": v(208.67, 215.6) * mm});
            skLineSegment(sketch, "E121.7.5", {"start": v(208.53, 201.6) * mm, "end": v(215.6, 208.67) * mm});
            skLineSegment(sketch, "E121.7.6", {"start": v(212.84, 212.84) * mm, "end": v(212.84, 211.42) * mm});
            skLineSegment(sketch, "E121.7.7", {"start": v(204.35, 204.35) * mm, "end": v(205.77, 204.35) * mm});
            skLineSegment(sketch, "E121.7.8", {"start": v(204.35, 204.35) * mm, "end": v(204.35, 205.77) * mm});
            skLineSegment(sketch, "E121.7.9", {"start": v(212.84, 212.84) * mm, "end": v(211.42, 212.84) * mm});
            skSolve(sketch);
        }
        {
            var Q0;
            Q0=qSketchRegion(id+"F6",true);
            extrude(context, id + "F7", {"entities" : qUnion([Q0]), "depth" : 10 * mm, "offsetDistance" : 25 * mm});
        }
        {
            var Q0;
            Q0=qCreatedBy(id+"F1.planeOp",FACE);
            var sketch = newSketch(context, id + "F8", { "sketchPlane" : qUnion([Q0])});
            skCircle(sketch, "E122", {"center": v(0, 0) * mm, "radius": 575 * mm});
            skLineSegment(sketch, "E123.bottom", {"start": v(4.9, 530) * mm, "end": v(1, 530) * mm});
            skLineSegment(sketch, "E123.top", {"start": v(4.9, 540) * mm, "end": v(1, 540) * mm});
            skLineSegment(sketch, "E123.left", {"start": v(4.9, 530) * mm, "end": v(4.9, 540) * mm});
            skLineSegment(sketch, "E123.right", {"start": v(-4.9, 530) * mm, "end": v(-4.9, 540) * mm});
            skPoint(sketch, "E123.middle", {"position": v(0, 535) * mm});
            skLineSegment(sketch, "E124", {"start": v(0, 541) * mm, "end": v(-1, 540) * mm});
            skLineSegment(sketch, "E125", {"start": v(0, 541) * mm, "end": v(1, 540) * mm});
            skLineSegment(sketch, "E126.trimOffspring", {"start": v(-1, 540) * mm, "end": v(-4.9, 540) * mm});
            skLineSegment(sketch, "E127", {"start": v(0, 529) * mm, "end": v(-1, 530) * mm});
            skLineSegment(sketch, "E128", {"start": v(0, 529) * mm, "end": v(1, 530) * mm});
            skLineSegment(sketch, "E129.trimOffspring", {"start": v(-1, 530) * mm, "end": v(-4.9, 530) * mm});
            skPoint(sketch, "E130.2.0", {"position": v(-378.3, 378.3) * mm});
            skLineSegment(sketch, "E130.2.1", {"start": v(-378.23, 371.3) * mm, "end": v(-385.3, 378.37) * mm});
            skLineSegment(sketch, "E130.2.2", {"start": v(-371.3, 378.23) * mm, "end": v(-378.37, 385.3) * mm});
            skLineSegment(sketch, "E130.2.3", {"start": v(-371.3, 378.23) * mm, "end": v(-374.06, 375.47) * mm});
            skLineSegment(sketch, "E130.2.4", {"start": v(-374.06, 374.06) * mm, "end": v(-374.06, 375.47) * mm});
            skLineSegment(sketch, "E130.2.5", {"start": v(-374.06, 374.06) * mm, "end": v(-375.47, 374.06) * mm});
            skLineSegment(sketch, "E130.2.6", {"start": v(-375.47, 374.06) * mm, "end": v(-378.23, 371.3) * mm});
            skLineSegment(sketch, "E130.2.7", {"start": v(-378.37, 385.3) * mm, "end": v(-381.13, 382.54) * mm});
            skLineSegment(sketch, "E130.2.8", {"start": v(-382.54, 381.13) * mm, "end": v(-385.3, 378.37) * mm});
            skLineSegment(sketch, "E130.2.9", {"start": v(-382.54, 382.54) * mm, "end": v(-381.13, 382.54) * mm});
            skLineSegment(sketch, "E130.2.10", {"start": v(-382.54, 382.54) * mm, "end": v(-382.54, 381.13) * mm});
            skPoint(sketch, "E130.4.0", {"position": v(-535, 0) * mm});
            skLineSegment(sketch, "E130.4.1", {"start": v(-530, -4.9) * mm, "end": v(-540, -4.9) * mm});
            skLineSegment(sketch, "E130.4.2", {"start": v(-530, 4.9) * mm, "end": v(-540, 4.9) * mm});
            skLineSegment(sketch, "E130.4.3", {"start": v(-530, 4.9) * mm, "end": v(-530, 1) * mm});
            skLineSegment(sketch, "E130.4.4", {"start": v(-529, 0) * mm, "end": v(-530, 1) * mm});
            skLineSegment(sketch, "E130.4.5", {"start": v(-529, 0) * mm, "end": v(-530, -1) * mm});
            skLineSegment(sketch, "E130.4.6", {"start": v(-530, -1) * mm, "end": v(-530, -4.9) * mm});
            skLineSegment(sketch, "E130.4.7", {"start": v(-540, 4.9) * mm, "end": v(-540, 1) * mm});
            skLineSegment(sketch, "E130.4.8", {"start": v(-540, -1) * mm, "end": v(-540, -4.9) * mm});
            skLineSegment(sketch, "E130.4.9", {"start": v(-541, 0) * mm, "end": v(-540, 1) * mm});
            skLineSegment(sketch, "E130.4.10", {"start": v(-541, 0) * mm, "end": v(-540, -1) * mm});
            skPoint(sketch, "E130.6.0", {"position": v(-378.3, -378.3) * mm});
            skLineSegment(sketch, "E130.6.1", {"start": v(-371.3, -378.23) * mm, "end": v(-378.37, -385.3) * mm});
            skLineSegment(sketch, "E130.6.2", {"start": v(-378.23, -371.3) * mm, "end": v(-385.3, -378.37) * mm});
            skLineSegment(sketch, "E130.6.3", {"start": v(-378.23, -371.3) * mm, "end": v(-375.47, -374.06) * mm});
            skLineSegment(sketch, "E130.6.4", {"start": v(-374.06, -374.06) * mm, "end": v(-375.47, -374.06) * mm});
            skLineSegment(sketch, "E130.6.5", {"start": v(-374.06, -374.06) * mm, "end": v(-374.06, -375.47) * mm});
            skLineSegment(sketch, "E130.6.6", {"start": v(-374.06, -375.47) * mm, "end": v(-371.3, -378.23) * mm});
            skLineSegment(sketch, "E130.6.7", {"start": v(-385.3, -378.37) * mm, "end": v(-382.54, -381.13) * mm});
            skLineSegment(sketch, "E130.6.8", {"start": v(-381.13, -382.54) * mm, "end": v(-378.37, -385.3) * mm});
            skLineSegment(sketch, "E130.6.9", {"start": v(-382.54, -382.54) * mm, "end": v(-382.54, -381.13) * mm});
            skLineSegment(sketch, "E130.6.10", {"start": v(-382.54, -382.54) * mm, "end": v(-381.13, -382.54) * mm});
            skPoint(sketch, "E130.8.0", {"position": v(0, -535) * mm});
            skLineSegment(sketch, "E130.8.1", {"start": v(4.9, -530) * mm, "end": v(4.9, -540) * mm});
            skLineSegment(sketch, "E130.8.2", {"start": v(-4.9, -530) * mm, "end": v(-4.9, -540) * mm});
            skLineSegment(sketch, "E130.8.3", {"start": v(-4.9, -530) * mm, "end": v(-1, -530) * mm});
            skLineSegment(sketch, "E130.8.4", {"start": v(0, -529) * mm, "end": v(-1, -530) * mm});
            skLineSegment(sketch, "E130.8.5", {"start": v(0, -529) * mm, "end": v(1, -530) * mm});
            skLineSegment(sketch, "E130.8.6", {"start": v(1, -530) * mm, "end": v(4.9, -530) * mm});
            skLineSegment(sketch, "E130.8.7", {"start": v(-4.9, -540) * mm, "end": v(-1, -540) * mm});
            skLineSegment(sketch, "E130.8.8", {"start": v(1, -540) * mm, "end": v(4.9, -540) * mm});
            skLineSegment(sketch, "E130.8.9", {"start": v(0, -541) * mm, "end": v(-1, -540) * mm});
            skLineSegment(sketch, "E130.8.10", {"start": v(0, -541) * mm, "end": v(1, -540) * mm});
            skPoint(sketch, "E130.10.0", {"position": v(378.3, -378.3) * mm});
            skLineSegment(sketch, "E130.10.1", {"start": v(378.23, -371.3) * mm, "end": v(385.3, -378.37) * mm});
            skLineSegment(sketch, "E130.10.2", {"start": v(371.3, -378.23) * mm, "end": v(378.37, -385.3) * mm});
            skLineSegment(sketch, "E130.10.3", {"start": v(371.3, -378.23) * mm, "end": v(374.06, -375.47) * mm});
            skLineSegment(sketch, "E130.10.4", {"start": v(374.06, -374.06) * mm, "end": v(374.06, -375.47) * mm});
            skLineSegment(sketch, "E130.10.5", {"start": v(374.06, -374.06) * mm, "end": v(375.47, -374.06) * mm});
            skLineSegment(sketch, "E130.10.6", {"start": v(375.47, -374.06) * mm, "end": v(378.23, -371.3) * mm});
            skLineSegment(sketch, "E130.10.7", {"start": v(378.37, -385.3) * mm, "end": v(381.13, -382.54) * mm});
            skLineSegment(sketch, "E130.10.8", {"start": v(382.54, -381.13) * mm, "end": v(385.3, -378.37) * mm});
            skLineSegment(sketch, "E130.10.9", {"start": v(382.54, -382.54) * mm, "end": v(381.13, -382.54) * mm});
            skLineSegment(sketch, "E130.10.10", {"start": v(382.54, -382.54) * mm, "end": v(382.54, -381.13) * mm});
            skPoint(sketch, "E130.12.0", {"position": v(535, 0) * mm});
            skLineSegment(sketch, "E130.12.1", {"start": v(530, 4.9) * mm, "end": v(540, 4.9) * mm});
            skLineSegment(sketch, "E130.12.2", {"start": v(530, -4.9) * mm, "end": v(540, -4.9) * mm});
            skLineSegment(sketch, "E130.12.3", {"start": v(530, -4.9) * mm, "end": v(530, -1) * mm});
            skLineSegment(sketch, "E130.12.4", {"start": v(529, 0) * mm, "end": v(530, -1) * mm});
            skLineSegment(sketch, "E130.12.5", {"start": v(529, 0) * mm, "end": v(530, 1) * mm});
            skLineSegment(sketch, "E130.12.6", {"start": v(530, 1) * mm, "end": v(530, 4.9) * mm});
            skLineSegment(sketch, "E130.12.7", {"start": v(540, -4.9) * mm, "end": v(540, -1) * mm});
            skLineSegment(sketch, "E130.12.8", {"start": v(540, 1) * mm, "end": v(540, 4.9) * mm});
            skLineSegment(sketch, "E130.12.9", {"start": v(541, 0) * mm, "end": v(540, -1) * mm});
            skLineSegment(sketch, "E130.12.10", {"start": v(541, 0) * mm, "end": v(540, 1) * mm});
            skPoint(sketch, "E130.14.0", {"position": v(378.3, 378.3) * mm});
            skLineSegment(sketch, "E130.14.1", {"start": v(371.3, 378.23) * mm, "end": v(378.37, 385.3) * mm});
            skLineSegment(sketch, "E130.14.2", {"start": v(378.23, 371.3) * mm, "end": v(385.3, 378.37) * mm});
            skLineSegment(sketch, "E130.14.3", {"start": v(378.23, 371.3) * mm, "end": v(375.47, 374.06) * mm});
            skLineSegment(sketch, "E130.14.4", {"start": v(374.06, 374.06) * mm, "end": v(375.47, 374.06) * mm});
            skLineSegment(sketch, "E130.14.5", {"start": v(374.06, 374.06) * mm, "end": v(374.06, 375.47) * mm});
            skLineSegment(sketch, "E130.14.6", {"start": v(374.06, 375.47) * mm, "end": v(371.3, 378.23) * mm});
            skLineSegment(sketch, "E130.14.7", {"start": v(385.3, 378.37) * mm, "end": v(382.54, 381.13) * mm});
            skLineSegment(sketch, "E130.14.8", {"start": v(381.13, 382.54) * mm, "end": v(378.37, 385.3) * mm});
            skLineSegment(sketch, "E130.14.9", {"start": v(382.54, 382.54) * mm, "end": v(382.54, 381.13) * mm});
            skLineSegment(sketch, "E130.14.10", {"start": v(382.54, 382.54) * mm, "end": v(381.13, 382.54) * mm});
            skCircle(sketch, "E131", {"center": v(0, 0) * mm, "radius": 500 * mm});
            skSolve(sketch);
        }
        {
            var Q0;
            Q0=qSketchRegion(id+"F8",true);
            extrude(context, id + "F9", {"entities" : qUnion([Q0]), "depth" : 10 * mm, "offsetDistance" : 25 * mm});
        }
        {
            var Q0;
            Q0=qCreatedBy(makeId("Right.planeOp"),FACE);
            var sketch = newSketch(context, id + "F10", { "sketchPlane" : qUnion([Q0])});
            skLineSegment(sketch, "E132.0.1", {"start": v(540, 0) * mm, "end": v(540, 10) * mm});
            skLineSegment(sketch, "E132.0.2", {"start": v(540, 10) * mm, "end": v(530, 10) * mm});
            skLineSegment(sketch, "E132.0.3", {"start": v(530, 10) * mm, "end": v(530, 0) * mm});
            skLineSegment(sketch, "E133.0.0", {"start": v(530, -200) * mm, "end": v(540, -200) * mm});
            skLineSegment(sketch, "E133.0.1", {"start": v(540, -200) * mm, "end": v(540, -190) * mm});
            skLineSegment(sketch, "E133.0.3", {"start": v(530, -190) * mm, "end": v(530, -200) * mm});
            skLineSegment(sketch, "E134", {"start": v(530, 0) * mm, "end": v(520, 0) * mm});
            skLineSegment(sketch, "E135", {"start": v(520, 0) * mm, "end": v(520, -90.1) * mm});
            skLineSegment(sketch, "E136", {"start": v(520, -190) * mm, "end": v(530, -190) * mm});
            skLineSegment(sketch, "E137", {"start": v(540, -190) * mm, "end": v(550, -190) * mm});
            skLineSegment(sketch, "E138", {"start": v(550, -190) * mm, "end": v(550, 0) * mm});
            skLineSegment(sketch, "E139", {"start": v(550, 0) * mm, "end": v(540, 0) * mm});
            skLineSegment(sketch, "E140.0.0", {"start": v(290, 0) * mm, "end": v(300, 0) * mm});
            skLineSegment(sketch, "E140.0.1", {"start": v(300, 0) * mm, "end": v(300, 10) * mm});
            skLineSegment(sketch, "E140.0.3", {"start": v(290, 10) * mm, "end": v(290, 0) * mm});
            skLineSegment(sketch, "E141.0.1", {"start": v(300, 200) * mm, "end": v(300, 210) * mm});
            skLineSegment(sketch, "E141.0.2", {"start": v(300, 210) * mm, "end": v(290, 210) * mm});
            skLineSegment(sketch, "E141.0.3", {"start": v(290, 210) * mm, "end": v(290, 200) * mm});
            skLineSegment(sketch, "E142", {"start": v(290, 200) * mm, "end": v(280, 200) * mm});
            skLineSegment(sketch, "E143", {"start": v(280, 200) * mm, "end": v(280, 109.9) * mm});
            skLineSegment(sketch, "E144", {"start": v(280, 10) * mm, "end": v(290, 10) * mm});
            skLineSegment(sketch, "E145", {"start": v(300, 10) * mm, "end": v(310, 10) * mm});
            skLineSegment(sketch, "E146", {"start": v(310, 10) * mm, "end": v(310, 200) * mm});
            skLineSegment(sketch, "E147", {"start": v(310, 200) * mm, "end": v(300, 200) * mm});
            skLineSegment(sketch, "E148", {"start": v(280, 109.9) * mm, "end": v(290, 109.9) * mm});
            skLineSegment(sketch, "E149", {"start": v(290, 109.9) * mm, "end": v(290, 100.1) * mm});
            skLineSegment(sketch, "E150", {"start": v(290, 100.1) * mm, "end": v(280, 100.1) * mm});
            skLineSegment(sketch, "E151.trimOffspring", {"start": v(280, 100.1) * mm, "end": v(280, 10) * mm});
            skLineSegment(sketch, "E152", {"start": v(520, -90.1) * mm, "end": v(530, -90.1) * mm});
            skLineSegment(sketch, "E153", {"start": v(530, -90.1) * mm, "end": v(530, -99.9) * mm});
            skLineSegment(sketch, "E154", {"start": v(530, -99.9) * mm, "end": v(520, -99.9) * mm});
            skLineSegment(sketch, "E155.trimOffspring", {"start": v(520, -99.9) * mm, "end": v(520, -190) * mm});
            skSolve(sketch);
        }
        {
            var Q0;
            Q0=qSketchRegion(id+"F10",true);
            extrude(context, id + "F11", {"entities" : qUnion([Q0]), "endBound" : BoundingType.SYMMETRIC, "depth" : 10 * mm, "offsetDistance" : 25 * mm});
        }
        {
            var Q0;
            Q0=makeQuery(id+"F11.opExtrude","SWEPT_BODY",BODY,{"disambiguationData":[OSD([sQuery(id+"F10.wireOp",EDGE,"E132.0.1"),sQuery(id+"F10.wireOp",EDGE,"E132.0.2"),sQuery(id+"F10.wireOp",EDGE,"E132.0.3"),sQuery(id+"F10.wireOp",EDGE,"E133.0.0"),sQuery(id+"F10.wireOp",EDGE,"E133.0.1"),sQuery(id+"F10.wireOp",EDGE,"E133.0.3"),sQuery(id+"F10.wireOp",EDGE,"E134"),sQuery(id+"F10.wireOp",EDGE,"E135"),sQuery(id+"F10.wireOp",EDGE,"E136"),sQuery(id+"F10.wireOp",EDGE,"E137"),sQuery(id+"F10.wireOp",EDGE,"E138"),sQuery(id+"F10.wireOp",EDGE,"E139")])]});
            var Q1;
            Q1=makeQuery(id+"F11.opExtrude","SWEPT_BODY",BODY,{"disambiguationData":[OSD([sQuery(id+"F10.wireOp",EDGE,"E140.0.0"),sQuery(id+"F10.wireOp",EDGE,"E140.0.1"),sQuery(id+"F10.wireOp",EDGE,"E140.0.3"),sQuery(id+"F10.wireOp",EDGE,"E141.0.1"),sQuery(id+"F10.wireOp",EDGE,"E141.0.2"),sQuery(id+"F10.wireOp",EDGE,"E141.0.3"),sQuery(id+"F10.wireOp",EDGE,"E142"),sQuery(id+"F10.wireOp",EDGE,"E143"),sQuery(id+"F10.wireOp",EDGE,"E144"),sQuery(id+"F10.wireOp",EDGE,"E145"),sQuery(id+"F10.wireOp",EDGE,"E146"),sQuery(id+"F10.wireOp",EDGE,"E147")])]});
            var Q2;
            Q2=makeQuery(id+"F7.opExtrude","CAP_EDGE",EDGE,{"disambiguationData":[OSD([sQuery(id+"F6.wireOp",EDGE,"E70.0")])],"isStart":false});
            circularPattern(context, id + "F12", {"operationType" : NewBodyOperationType.ADD, "entities" : qUnion([Q0, Q1]), "axis" : qUnion([Q2]), "angle" : 360 * degree, "instanceCount" : 8, "equalSpace" : true});
        }
        {
            var Q0;
            Q0=qCreatedBy(id+"F2.planeOp",FACE);
            var sketch = newSketch(context, id + "F13", { "sketchPlane" : qUnion([Q0])});
            skPoint(sketch, "E156.0", {"position": v(-520, 0) * mm});
            skPoint(sketch, "E157.0", {"position": v(-540, 0) * mm});
            skPoint(sketch, "E158.0", {"position": v(-530, -5) * mm});
            skPoint(sketch, "E159.0", {"position": v(-530, 5) * mm});
            skArc(sketch, "E160", {"start": v(-539.98, -5) * mm, "mid": v(-498.9, -206.65) * mm, "end": v(-385.36, -378.29) * mm});
            skCircle(sketch, "E161", {"center": v(0, 0) * mm, "radius": 520 * mm});
            skLineSegment(sketch, "E162", {"start": v(-530, 5) * mm, "end": v(-530, -5) * mm});
            skLineSegment(sketch, "E163", {"start": v(-530, 5) * mm, "end": v(-539.98, 5) * mm});
            skLineSegment(sketch, "E164", {"start": v(-530, -5) * mm, "end": v(-539.98, -5) * mm});
            skLineSegment(sketch, "E165", {"start": v(-540, 0) * mm, "end": v(-520, 0) * mm, "construction": true});
            skLineSegment(sketch, "E166.1.0", {"start": v(-378.3, -371.23) * mm, "end": v(-385.36, -378.29) * mm});
            skLineSegment(sketch, "E166.1.1", {"start": v(-378.3, -371.23) * mm, "end": v(-371.23, -378.3) * mm});
            skLineSegment(sketch, "E166.1.2", {"start": v(-381.84, -381.84) * mm, "end": v(-367.7, -367.7) * mm, "construction": true});
            skLineSegment(sketch, "E166.1.3", {"start": v(-371.23, -378.3) * mm, "end": v(-378.29, -385.36) * mm});
            skLineSegment(sketch, "E166.2.0", {"start": v(-5, -530) * mm, "end": v(-5, -539.98) * mm});
            skLineSegment(sketch, "E166.2.1", {"start": v(-5, -530) * mm, "end": v(5, -530) * mm});
            skLineSegment(sketch, "E166.2.2", {"start": v(0, -540) * mm, "end": v(0, -520) * mm, "construction": true});
            skLineSegment(sketch, "E166.2.3", {"start": v(5, -530) * mm, "end": v(5, -539.98) * mm});
            skLineSegment(sketch, "E166.3.0", {"start": v(371.23, -378.3) * mm, "end": v(378.29, -385.36) * mm});
            skLineSegment(sketch, "E166.3.1", {"start": v(371.23, -378.3) * mm, "end": v(378.3, -371.23) * mm});
            skLineSegment(sketch, "E166.3.2", {"start": v(381.84, -381.84) * mm, "end": v(367.7, -367.7) * mm, "construction": true});
            skLineSegment(sketch, "E166.3.3", {"start": v(378.3, -371.23) * mm, "end": v(385.36, -378.29) * mm});
            skLineSegment(sketch, "E166.4.0", {"start": v(530, -5) * mm, "end": v(539.98, -5) * mm});
            skLineSegment(sketch, "E166.4.1", {"start": v(530, -5) * mm, "end": v(530, 5) * mm});
            skLineSegment(sketch, "E166.4.2", {"start": v(540, 0) * mm, "end": v(520, 0) * mm, "construction": true});
            skLineSegment(sketch, "E166.4.3", {"start": v(530, 5) * mm, "end": v(539.98, 5) * mm});
            skLineSegment(sketch, "E166.5.0", {"start": v(378.3, 371.23) * mm, "end": v(385.36, 378.29) * mm});
            skLineSegment(sketch, "E166.5.1", {"start": v(378.3, 371.23) * mm, "end": v(371.23, 378.3) * mm});
            skLineSegment(sketch, "E166.5.2", {"start": v(381.84, 381.84) * mm, "end": v(367.7, 367.7) * mm, "construction": true});
            skLineSegment(sketch, "E166.5.3", {"start": v(371.23, 378.3) * mm, "end": v(378.29, 385.36) * mm});
            skLineSegment(sketch, "E166.6.0", {"start": v(5, 530) * mm, "end": v(5, 539.98) * mm});
            skLineSegment(sketch, "E166.6.1", {"start": v(5, 530) * mm, "end": v(-5, 530) * mm});
            skLineSegment(sketch, "E166.6.2", {"start": v(0, 540) * mm, "end": v(0, 520) * mm, "construction": true});
            skLineSegment(sketch, "E166.6.3", {"start": v(-5, 530) * mm, "end": v(-5, 539.98) * mm});
            skLineSegment(sketch, "E166.7.0", {"start": v(-371.23, 378.3) * mm, "end": v(-378.29, 385.36) * mm});
            skLineSegment(sketch, "E166.7.1", {"start": v(-371.23, 378.3) * mm, "end": v(-378.3, 371.23) * mm});
            skLineSegment(sketch, "E166.7.2", {"start": v(-381.84, 381.84) * mm, "end": v(-367.7, 367.7) * mm, "construction": true});
            skLineSegment(sketch, "E166.7.3", {"start": v(-378.3, 371.23) * mm, "end": v(-385.36, 378.29) * mm});
            skArc(sketch, "E167.trimOffspring", {"start": v(-385.36, 378.29) * mm, "mid": v(-498.9, 206.65) * mm, "end": v(-539.98, 5) * mm});
            skArc(sketch, "E168.trimOffspring", {"start": v(-5, 539.98) * mm, "mid": v(-206.65, 498.9) * mm, "end": v(-378.29, 385.36) * mm});
            skArc(sketch, "E169.trimOffspring", {"start": v(378.29, 385.36) * mm, "mid": v(206.65, 498.9) * mm, "end": v(5, 539.98) * mm});
            skArc(sketch, "E170.trimOffspring", {"start": v(539.98, 5) * mm, "mid": v(498.9, 206.65) * mm, "end": v(385.36, 378.29) * mm});
            skArc(sketch, "E171.trimOffspring", {"start": v(385.36, -378.29) * mm, "mid": v(498.9, -206.65) * mm, "end": v(539.98, -5) * mm});
            skArc(sketch, "E172.trimOffspring", {"start": v(5, -539.98) * mm, "mid": v(206.65, -498.9) * mm, "end": v(378.29, -385.36) * mm});
            skArc(sketch, "E173.trimOffspring", {"start": v(-378.29, -385.36) * mm, "mid": v(-206.65, -498.9) * mm, "end": v(-5, -539.98) * mm});
            skSolve(sketch);
        }
        {
            var Q0;
            Q0=qSketchRegion(id+"F13",true);
            extrude(context, id + "F14", {"entities" : qUnion([Q0]), "depth" : 10 * mm, "offsetDistance" : 25 * mm});
        }
        {
            var Q0;
            Q0=qCreatedBy(id+"F3.planeOp",FACE);
            var sketch = newSketch(context, id + "F15", { "sketchPlane" : qUnion([Q0])});
            skPoint(sketch, "E174.0", {"position": v(-280, 0) * mm});
            skPoint(sketch, "E175.0", {"position": v(-290, -5) * mm});
            skPoint(sketch, "E176.0", {"position": v(-290, 5) * mm});
            skPoint(sketch, "E177.0", {"position": v(-300, 0) * mm});
            skArc(sketch, "E178", {"start": v(-299.96, -5) * mm, "mid": v(-277.16, -114.8) * mm, "end": v(-215.64, -208.57) * mm});
            skCircle(sketch, "E179", {"center": v(0, 0) * mm, "radius": 280 * mm});
            skLineSegment(sketch, "E180", {"start": v(-290, 5) * mm, "end": v(-290, -5) * mm});
            skLineSegment(sketch, "E181", {"start": v(-290, -5) * mm, "end": v(-299.96, -5) * mm});
            skLineSegment(sketch, "E182", {"start": v(-290, 5) * mm, "end": v(-299.96, 5) * mm});
            skLineSegment(sketch, "E183.1.0", {"start": v(-208.6, -201.53) * mm, "end": v(-215.64, -208.57) * mm});
            skLineSegment(sketch, "E183.1.1", {"start": v(-208.6, -201.53) * mm, "end": v(-201.53, -208.6) * mm});
            skLineSegment(sketch, "E183.1.2", {"start": v(-201.53, -208.6) * mm, "end": v(-208.57, -215.64) * mm});
            skLineSegment(sketch, "E183.2.0", {"start": v(-5, -290) * mm, "end": v(-5, -299.96) * mm});
            skLineSegment(sketch, "E183.2.1", {"start": v(-5, -290) * mm, "end": v(5, -290) * mm});
            skLineSegment(sketch, "E183.2.2", {"start": v(5, -290) * mm, "end": v(5, -299.96) * mm});
            skLineSegment(sketch, "E183.3.0", {"start": v(201.53, -208.6) * mm, "end": v(208.57, -215.64) * mm});
            skLineSegment(sketch, "E183.3.1", {"start": v(201.53, -208.6) * mm, "end": v(208.6, -201.53) * mm});
            skLineSegment(sketch, "E183.3.2", {"start": v(208.6, -201.53) * mm, "end": v(215.64, -208.57) * mm});
            skLineSegment(sketch, "E183.4.0", {"start": v(290, -5) * mm, "end": v(299.96, -5) * mm});
            skLineSegment(sketch, "E183.4.1", {"start": v(290, -5) * mm, "end": v(290, 5) * mm});
            skLineSegment(sketch, "E183.4.2", {"start": v(290, 5) * mm, "end": v(299.96, 5) * mm});
            skLineSegment(sketch, "E183.5.0", {"start": v(208.6, 201.53) * mm, "end": v(215.64, 208.57) * mm});
            skLineSegment(sketch, "E183.5.1", {"start": v(208.6, 201.53) * mm, "end": v(201.53, 208.6) * mm});
            skLineSegment(sketch, "E183.5.2", {"start": v(201.53, 208.6) * mm, "end": v(208.57, 215.64) * mm});
            skLineSegment(sketch, "E183.6.0", {"start": v(5, 290) * mm, "end": v(5, 299.96) * mm});
            skLineSegment(sketch, "E183.6.1", {"start": v(5, 290) * mm, "end": v(-5, 290) * mm});
            skLineSegment(sketch, "E183.6.2", {"start": v(-5, 290) * mm, "end": v(-5, 299.96) * mm});
            skLineSegment(sketch, "E183.7.0", {"start": v(-201.53, 208.6) * mm, "end": v(-208.57, 215.64) * mm});
            skLineSegment(sketch, "E183.7.1", {"start": v(-201.53, 208.6) * mm, "end": v(-208.6, 201.53) * mm});
            skLineSegment(sketch, "E183.7.2", {"start": v(-208.6, 201.53) * mm, "end": v(-215.64, 208.57) * mm});
            skArc(sketch, "E184.trimOffspring", {"start": v(-215.64, 208.57) * mm, "mid": v(-277.16, 114.8) * mm, "end": v(-299.96, 5) * mm});
            skArc(sketch, "E185.trimOffspring", {"start": v(-5, 299.96) * mm, "mid": v(-114.8, 277.16) * mm, "end": v(-208.57, 215.64) * mm});
            skArc(sketch, "E186.trimOffspring", {"start": v(208.57, 215.64) * mm, "mid": v(114.8, 277.16) * mm, "end": v(5, 299.96) * mm});
            skArc(sketch, "E187.trimOffspring", {"start": v(299.96, 5) * mm, "mid": v(277.16, 114.8) * mm, "end": v(215.64, 208.57) * mm});
            skArc(sketch, "E188.trimOffspring", {"start": v(215.64, -208.57) * mm, "mid": v(277.16, -114.8) * mm, "end": v(299.96, -5) * mm});
            skArc(sketch, "E189.trimOffspring", {"start": v(5, -299.96) * mm, "mid": v(114.8, -277.16) * mm, "end": v(208.57, -215.64) * mm});
            skArc(sketch, "E190.trimOffspring", {"start": v(-208.57, -215.64) * mm, "mid": v(-114.8, -277.16) * mm, "end": v(-5, -299.96) * mm});
            skSolve(sketch);
        }
        {
            var Q0;
            Q0=qSketchRegion(id+"F15",true);
            extrude(context, id + "F16", {"entities" : qUnion([Q0]), "depth" : 10 * mm, "offsetDistance" : 25 * mm});
        }
    });
